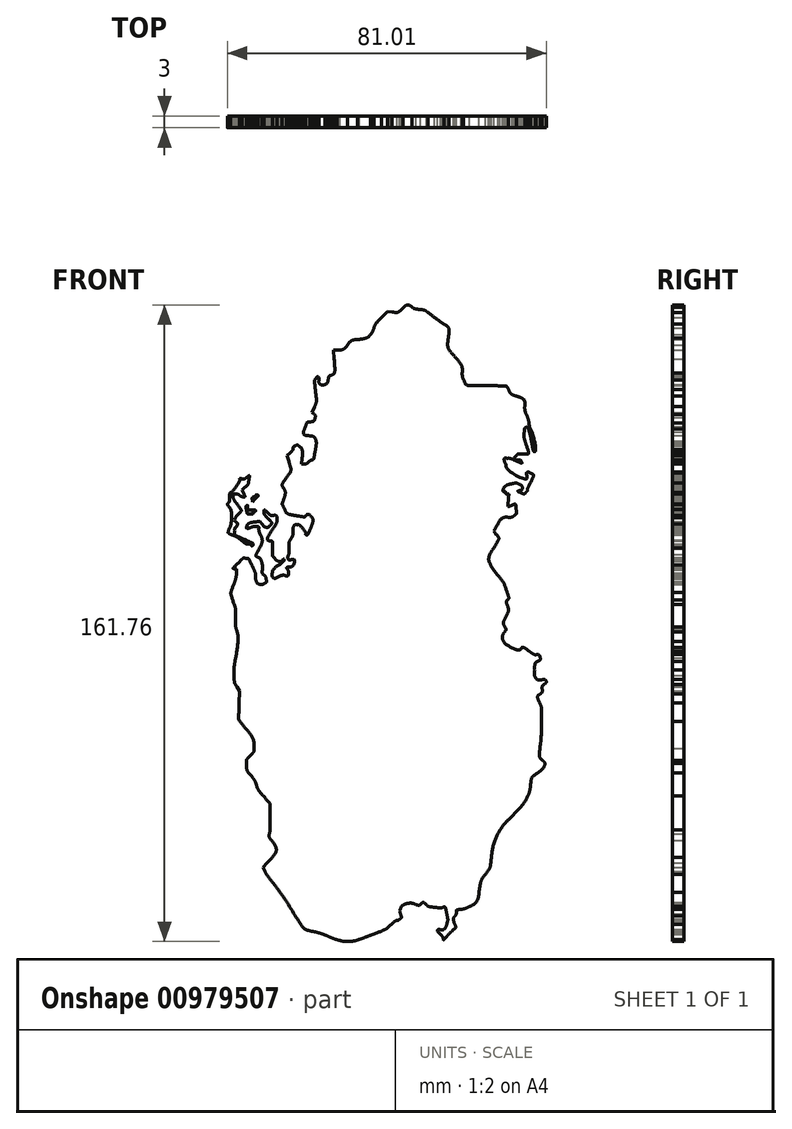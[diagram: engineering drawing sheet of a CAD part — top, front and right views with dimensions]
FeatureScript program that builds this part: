
annotation { "Feature Type Name" : "Feature", "Feature Type Description" : "" }
export const myFeature = defineFeature(function(context is Context, id is Id, definition is map)
    precondition{}
    {
        {
            var Q0;
            Q0=qCreatedBy(makeId("Front.planeOp"),FACE);
            var sketch = newSketch(context, id + "F0", { "sketchPlane" : qUnion([Q0])});
            skLineSegment(sketch, "E0", {"start": v(-32.88, 19.2) * mm, "end": v(-32.1, 20.83) * mm});
            skLineSegment(sketch, "E1", {"start": v(-32.1, 20.83) * mm, "end": v(-32.57, 22.16) * mm});
            skLineSegment(sketch, "E2", {"start": v(-27.5, 16.63) * mm, "end": v(-26.83, 16.28) * mm});
            skLineSegment(sketch, "E3", {"start": v(-26.83, 16.28) * mm, "end": v(-26.97, 16.83) * mm});
            skLineSegment(sketch, "E4", {"start": v(-24.85, 15.67) * mm, "end": v(-25.4, 15.88) * mm});
            skLineSegment(sketch, "E5", {"start": v(-25.4, 15.88) * mm, "end": v(-25.34, 18.4) * mm});
            skLineSegment(sketch, "E6", {"start": v(-1.75, 78.04) * mm, "end": v(-0.2, 79.6) * mm});
            skLineSegment(sketch, "E7", {"start": v(-0.2, 79.6) * mm, "end": v(1.27, 79.6) * mm});
            skLineSegment(sketch, "E8", {"start": v(38.3, 44.26) * mm, "end": v(38.3, 43.17) * mm});
            skLineSegment(sketch, "E9", {"start": v(38.3, 43.17) * mm, "end": v(37.62, 43.24) * mm});
            skLineSegment(sketch, "E10", {"start": v(39.65, -31.25) * mm, "end": v(39.52, -33.83) * mm});
            skLineSegment(sketch, "E11", {"start": v(39.52, -33.83) * mm, "end": v(40.18, -34.42) * mm});
            skLineSegment(sketch, "E12", {"start": v(1.4, 79.08) * mm, "end": v(0.3, 79.22) * mm});
            skLineSegment(sketch, "E13", {"start": v(0.3, 79.22) * mm, "end": v(-1.23, 77.67) * mm});
            skLineSegment(sketch, "E14", {"start": v(-12.51, 69.45) * mm, "end": v(-13.4, 69.45) * mm});
            skLineSegment(sketch, "E15", {"start": v(-13.4, 69.45) * mm, "end": v(-13.27, 67.07) * mm});
            skLineSegment(sketch, "E16", {"start": v(-18.31, 54.9) * mm, "end": v(-18.88, 53.48) * mm});
            skLineSegment(sketch, "E17", {"start": v(-18.88, 53.48) * mm, "end": v(-18.43, 53.1) * mm});
            skLineSegment(sketch, "E18", {"start": v(-20.94, 40.45) * mm, "end": v(-21.55, 40.45) * mm});
            skLineSegment(sketch, "E19", {"start": v(-21.55, 40.45) * mm, "end": v(-21.44, 41.8) * mm});
            skLineSegment(sketch, "E20", {"start": v(-24.47, 43.3) * mm, "end": v(-25.23, 42.61) * mm});
            skLineSegment(sketch, "E21", {"start": v(-25.23, 42.61) * mm, "end": v(-24.8, 41.05) * mm});
            skLineSegment(sketch, "E22", {"start": v(-37.96, -16.18) * mm, "end": v(-37.29, -17.23) * mm});
            skLineSegment(sketch, "E23", {"start": v(-37.29, -17.23) * mm, "end": v(-37.41, -20.41) * mm});
            skLineSegment(sketch, "E24", {"start": v(-30.4, -60.92) * mm, "end": v(-31.42, -62.04) * mm});
            skLineSegment(sketch, "E25", {"start": v(-31.42, -62.04) * mm, "end": v(-30.9, -63.02) * mm});
            skLineSegment(sketch, "E26", {"start": v(-36.35, 33.14) * mm, "end": v(-36.7, 33.88) * mm});
            skLineSegment(sketch, "E27", {"start": v(-36.7, 33.88) * mm, "end": v(-35.92, 34.57) * mm});
            skLineSegment(sketch, "E28", {"start": v(-34.09, 31.43) * mm, "end": v(-34.09, 30.84) * mm});
            skLineSegment(sketch, "E29", {"start": v(-34.09, 30.84) * mm, "end": v(-33.35, 31.56) * mm});
            skFitSpline(sketch, "E30", {"points": [v(-13.45, -80.7) * mm, v(-14.26, -80.4) * mm, v(-15.79, -79.86) * mm, v(-16.84, -79.51) * mm]});
            skFitSpline(sketch, "E31", {"points": [v(-16.84, -79.51) * mm, v(-20.43, -78.33) * mm, v(-20.6, -78.25) * mm, v(-21.55, -77.26) * mm]});
            skFitSpline(sketch, "E32", {"points": [v(-21.55, -77.26) * mm, v(-22.07, -76.72) * mm, v(-23.66, -74.52) * mm, v(-25.09, -72.37) * mm]});
            skFitSpline(sketch, "E33", {"points": [v(-25.09, -72.37) * mm, v(-26.52, -70.21) * mm, v(-28.36, -67.6) * mm, v(-29.19, -66.55) * mm]});
            skFitSpline(sketch, "E34", {"points": [v(-29.19, -66.55) * mm, v(-30.6, -64.76) * mm, v(-31.97, -62.53) * mm, v(-31.97, -62.03) * mm]});
            skFitSpline(sketch, "E35", {"points": [v(-31.97, -62.03) * mm, v(-31.97, -61.91) * mm, v(-31.5, -61.27) * mm, v(-30.92, -60.6) * mm]});
            skFitSpline(sketch, "E36", {"points": [v(-30.92, -60.6) * mm, v(-29.85, -59.39) * mm, v(-29, -57.92) * mm, v(-29, -57.28) * mm]});
            skFitSpline(sketch, "E37", {"points": [v(-29, -57.28) * mm, v(-29, -57.08) * mm, v(-29.34, -56.3) * mm, v(-29.75, -55.53) * mm]});
            skFitSpline(sketch, "E38", {"points": [v(-29.75, -55.53) * mm, v(-30.57, -53.98) * mm, v(-30.63, -53.57) * mm, v(-30.2, -52.72) * mm]});
            skFitSpline(sketch, "E39", {"points": [v(-30.2, -52.72) * mm, v(-29.95, -52.26) * mm, v(-29.92, -51.55) * mm, v(-30.04, -49.29) * mm]});
            skFitSpline(sketch, "E40", {"points": [v(-30.04, -49.29) * mm, v(-30.2, -46.13) * mm, v(-30.12, -46.32) * mm, v(-32.34, -43.6) * mm]});
            skFitSpline(sketch, "E41", {"points": [v(-32.34, -43.6) * mm, v(-32.83, -43) * mm, v(-33.38, -42.01) * mm, v(-33.55, -41.42) * mm]});
            skFitSpline(sketch, "E42", {"points": [v(-33.55, -41.42) * mm, v(-33.73, -40.84) * mm, v(-34.2, -39.94) * mm, v(-34.62, -39.44) * mm]});
            skFitSpline(sketch, "E43", {"points": [v(-34.62, -39.44) * mm, v(-36.03, -37.71) * mm, v(-36.52, -35.97) * mm, v(-35.98, -34.56) * mm]});
            skFitSpline(sketch, "E44", {"points": [v(-35.98, -34.56) * mm, v(-35.86, -34.24) * mm, v(-35.38, -33.57) * mm, v(-34.92, -33.07) * mm]});
            skFitSpline(sketch, "E45", {"points": [v(-34.92, -33.07) * mm, v(-33.97, -32.03) * mm, v(-34, -32.17) * mm, v(-34.37, -30.78) * mm]});
            skFitSpline(sketch, "E46", {"points": [v(-34.37, -30.78) * mm, v(-34.75, -29.38) * mm, v(-35.2, -28.53) * mm, v(-36.46, -26.88) * mm]});
            skFitSpline(sketch, "E47", {"points": [v(-36.46, -26.88) * mm, v(-37.04, -26.13) * mm, v(-37.61, -25.27) * mm, v(-37.73, -24.97) * mm]});
            skFitSpline(sketch, "E48", {"points": [v(-37.73, -24.97) * mm, v(-37.97, -24.39) * mm, v(-38.06, -21.07) * mm, v(-37.9, -18.8) * mm]});
            skFitSpline(sketch, "E49", {"points": [v(-37.9, -18.8) * mm, v(-37.82, -17.55) * mm, v(-37.87, -17.35) * mm, v(-38.39, -16.67) * mm]});
            skFitSpline(sketch, "E50", {"points": [v(-38.39, -16.67) * mm, v(-39.51, -15.19) * mm, v(-39.6, -12.77) * mm, v(-38.72, -7.81) * mm]});
            skFitSpline(sketch, "E51", {"points": [v(-38.72, -7.81) * mm, v(-38.24, -5.14) * mm, v(-38.31, -2.1) * mm, v(-38.87, -1) * mm]});
            skFitSpline(sketch, "E52", {"points": [v(-38.87, -1) * mm, v(-39.1, -0.56) * mm, v(-39.11, -0.29) * mm, v(-38.94, 0.17) * mm]});
            skFitSpline(sketch, "E53", {"points": [v(-38.94, 0.17) * mm, v(-38.62, 1) * mm, v(-38.87, 3.38) * mm, v(-39.5, 5.38) * mm]});
            skFitSpline(sketch, "E54", {"points": [v(-39.5, 5.38) * mm, v(-39.78, 6.29) * mm, v(-40.01, 7.26) * mm, v(-40.01, 7.54) * mm]});
            skFitSpline(sketch, "E55", {"points": [v(-40.01, 7.54) * mm, v(-40.01, 7.83) * mm, v(-39.68, 9.05) * mm, v(-39.27, 10.27) * mm]});
            skFitSpline(sketch, "E56", {"points": [v(-39.27, 10.27) * mm, v(-38.41, 12.85) * mm, v(-38.39, 13.06) * mm, v(-38.96, 13.2) * mm]});
            skFitSpline(sketch, "E57", {"points": [v(-38.96, 13.2) * mm, v(-39.71, 13.4) * mm, v(-39.48, 14.32) * mm, v(-38.38, 15.5) * mm]});
            skFitSpline(sketch, "E58", {"points": [v(-38.38, 15.5) * mm, v(-36.83, 17.16) * mm, v(-35.68, 17.57) * mm, v(-34.74, 16.8) * mm]});
            skFitSpline(sketch, "E59", {"points": [v(-34.74, 16.8) * mm, v(-34.08, 16.26) * mm, v(-32.77, 13.22) * mm, v(-32.66, 11.98) * mm]});
            skFitSpline(sketch, "E60", {"points": [v(-32.66, 11.98) * mm, v(-32.55, 10.86) * mm, v(-32.37, 10.61) * mm, v(-31.6, 10.6) * mm]});
            skFitSpline(sketch, "E61", {"points": [v(-31.6, 10.6) * mm, v(-31, 10.6) * mm, v(-30.96, 11.24) * mm, v(-31.55, 11.77) * mm]});
            skFitSpline(sketch, "E62", {"points": [v(-31.55, 11.77) * mm, v(-31.84, 12.03) * mm, v(-31.97, 12.42) * mm, v(-31.97, 13) * mm]});
            skFitSpline(sketch, "E63", {"points": [v(-31.97, 13) * mm, v(-31.97, 14.32) * mm, v(-32.62, 16.12) * mm, v(-33.18, 16.38) * mm]});
            skFitSpline(sketch, "E64", {"points": [v(-33.18, 16.38) * mm, v(-33.86, 16.69) * mm, v(-33.8, 17.27) * mm, v(-32.88, 19.2) * mm]});
            skFitSpline(sketch, "E65", {"points": [v(-32.57, 22.16) * mm, v(-32.82, 22.9) * mm, v(-33.03, 23.65) * mm, v(-33.03, 23.83) * mm]});
            skFitSpline(sketch, "E66", {"points": [v(-33.03, 23.83) * mm, v(-33.03, 24.1) * mm, v(-33.14, 24.14) * mm, v(-33.5, 24.01) * mm]});
            skFitSpline(sketch, "E67", {"points": [v(-33.5, 24.01) * mm, v(-33.77, 23.92) * mm, v(-34.4, 23.84) * mm, v(-34.93, 23.84) * mm]});
            skFitSpline(sketch, "E68", {"points": [v(-34.93, 23.84) * mm, v(-35.84, 23.83) * mm, v(-35.89, 23.86) * mm, v(-35.95, 24.48) * mm]});
            skFitSpline(sketch, "E69", {"points": [v(-35.95, 24.48) * mm, v(-36.05, 25.55) * mm, v(-34.78, 26.27) * mm, v(-32.78, 26.27) * mm]});
            skFitSpline(sketch, "E70", {"points": [v(-32.78, 26.27) * mm, v(-31.93, 26.27) * mm, v(-31.64, 26.16) * mm, v(-31.1, 25.65) * mm]});
            skFitSpline(sketch, "E71", {"points": [v(-31.1, 25.65) * mm, v(-30.75, 25.3) * mm, v(-30.32, 25.08) * mm, v(-30.15, 25.14) * mm]});
            skFitSpline(sketch, "E72", {"points": [v(-30.15, 25.14) * mm, v(-29.7, 25.31) * mm, v(-29.77, 25.47) * mm, v(-30.7, 26.37) * mm]});
            skFitSpline(sketch, "E73", {"points": [v(-30.7, 26.37) * mm, v(-31.5, 27.15) * mm, v(-31.55, 27.27) * mm, v(-31.55, 28.43) * mm]});
            skFitSpline(sketch, "E74", {"points": [v(-31.55, 28.43) * mm, v(-31.55, 29.6) * mm, v(-31.52, 29.65) * mm, v(-31.02, 29.65) * mm]});
            skFitSpline(sketch, "E75", {"points": [v(-31.02, 29.65) * mm, v(-30.7, 29.65) * mm, v(-30.49, 29.53) * mm, v(-30.49, 29.36) * mm]});
            skFitSpline(sketch, "E76", {"points": [v(-30.49, 29.36) * mm, v(-30.49, 28.94) * mm, v(-28.82, 27.75) * mm, v(-28.24, 27.75) * mm]});
            skFitSpline(sketch, "E77", {"points": [v(-28.24, 27.75) * mm, v(-27.83, 27.75) * mm, v(-27.75, 27.6) * mm, v(-27.62, 26.6) * mm]});
            skFitSpline(sketch, "E78", {"points": [v(-27.62, 26.6) * mm, v(-27.46, 25.26) * mm, v(-27.66, 24.55) * mm, v(-28.57, 23.22) * mm]});
            skFitSpline(sketch, "E79", {"points": [v(-28.57, 23.22) * mm, v(-29.21, 22.29) * mm, v(-29.4, 21.61) * mm, v(-29.02, 21.61) * mm]});
            skFitSpline(sketch, "E80", {"points": [v(-29.02, 21.61) * mm, v(-28.66, 21.61) * mm, v(-28.35, 20.18) * mm, v(-28.49, 19.14) * mm]});
            skFitSpline(sketch, "E81", {"points": [v(-28.49, 19.14) * mm, v(-28.66, 17.84) * mm, v(-28.36, 17.07) * mm, v(-27.5, 16.63) * mm]});
            skFitSpline(sketch, "E82", {"points": [v(-26.97, 16.83) * mm, v(-27.1, 17.33) * mm, v(-27.05, 17.38) * mm, v(-26.5, 17.38) * mm]});
            skFitSpline(sketch, "E83", {"points": [v(-26.5, 17.38) * mm, v(-25.81, 17.38) * mm, v(-25.62, 17.08) * mm, v(-25.62, 16.04) * mm]});
            skFitSpline(sketch, "E84", {"points": [v(-25.62, 16.04) * mm, v(-25.62, 15.5) * mm, v(-25.82, 15.19) * mm, v(-26.56, 14.52) * mm]});
            skFitSpline(sketch, "E85", {"points": [v(-26.56, 14.52) * mm, v(-27.09, 14.05) * mm, v(-27.58, 13.4) * mm, v(-27.66, 13.06) * mm]});
            skFitSpline(sketch, "E86", {"points": [v(-27.66, 13.06) * mm, v(-27.79, 12.49) * mm, v(-27.76, 12.45) * mm, v(-27.3, 12.58) * mm]});
            skFitSpline(sketch, "E87", {"points": [v(-27.3, 12.58) * mm, v(-27.01, 12.65) * mm, v(-26.47, 12.72) * mm, v(-26.09, 12.72) * mm]});
            skFitSpline(sketch, "E88", {"points": [v(-26.09, 12.72) * mm, v(-25.47, 12.72) * mm, v(-25.42, 12.76) * mm, v(-25.61, 13.13) * mm]});
            skFitSpline(sketch, "E89", {"points": [v(-25.61, 13.13) * mm, v(-26.02, 13.88) * mm, v(-25.88, 14.6) * mm, v(-25.31, 14.75) * mm]});
            skFitSpline(sketch, "E90", {"points": [v(-25.31, 14.75) * mm, v(-25.03, 14.82) * mm, v(-24.68, 15.01) * mm, v(-24.55, 15.17) * mm]});
            skFitSpline(sketch, "E91", {"points": [v(-24.55, 15.17) * mm, v(-24.35, 15.4) * mm, v(-24.42, 15.5) * mm, v(-24.85, 15.67) * mm]});
            skFitSpline(sketch, "E92", {"points": [v(-25.34, 18.4) * mm, v(-25.28, 20.49) * mm, v(-25.2, 21.05) * mm, v(-24.84, 21.66) * mm]});
            skFitSpline(sketch, "E93", {"points": [v(-24.84, 21.66) * mm, v(-24.6, 22.07) * mm, v(-24.33, 22.91) * mm, v(-24.25, 23.54) * mm]});
            skFitSpline(sketch, "E94", {"points": [v(-24.25, 23.54) * mm, v(-24.05, 24.98) * mm, v(-23.67, 25.42) * mm, v(-22.64, 25.42) * mm]});
            skFitSpline(sketch, "E95", {"points": [v(-22.64, 25.42) * mm, v(-21.97, 25.42) * mm, v(-21.73, 25.28) * mm, v(-21.09, 24.54) * mm]});
            skFitSpline(sketch, "E96", {"points": [v(-21.09, 24.54) * mm, v(-20.67, 24.05) * mm, v(-20.32, 23.55) * mm, v(-20.32, 23.43) * mm]});
            skFitSpline(sketch, "E97", {"points": [v(-20.32, 23.43) * mm, v(-20.3, 22.93) * mm, v(-19.5, 25.15) * mm, v(-19.5, 25.74) * mm]});
            skFitSpline(sketch, "E98", {"points": [v(-19.5, 25.74) * mm, v(-19.48, 26.68) * mm, v(-19.75, 27) * mm, v(-20.27, 26.68) * mm]});
            skFitSpline(sketch, "E99", {"points": [v(-20.27, 26.68) * mm, v(-20.84, 26.32) * mm, v(-23.7, 26.75) * mm, v(-24.99, 27.38) * mm]});
            skFitSpline(sketch, "E100", {"points": [v(-24.99, 27.38) * mm, v(-26.7, 28.23) * mm, v(-27.27, 29.95) * mm, v(-26.55, 32.07) * mm]});
            skFitSpline(sketch, "E101", {"points": [v(-26.55, 32.07) * mm, v(-26.23, 33) * mm, v(-26.23, 33.13) * mm, v(-26.58, 33.9) * mm]});
            skFitSpline(sketch, "E102", {"points": [v(-26.58, 33.9) * mm, v(-27.04, 34.91) * mm, v(-26.9, 36) * mm, v(-26.2, 36.92) * mm]});
            skFitSpline(sketch, "E103", {"points": [v(-26.2, 36.92) * mm, v(-24.96, 38.54) * mm, v(-24.76, 39.42) * mm, v(-25.3, 40.73) * mm]});
            skFitSpline(sketch, "E104", {"points": [v(-25.3, 40.73) * mm, v(-25.48, 41.15) * mm, v(-25.62, 41.87) * mm, v(-25.62, 42.33) * mm]});
            skFitSpline(sketch, "E105", {"points": [v(-25.62, 42.33) * mm, v(-25.62, 43.02) * mm, v(-25.5, 43.25) * mm, v(-24.99, 43.62) * mm]});
            skFitSpline(sketch, "E106", {"points": [v(-24.99, 43.62) * mm, v(-24.64, 43.87) * mm, v(-24.35, 44.26) * mm, v(-24.35, 44.48) * mm]});
            skFitSpline(sketch, "E107", {"points": [v(-24.35, 44.48) * mm, v(-24.35, 45.6) * mm, v(-22.43, 46.16) * mm, v(-21.62, 45.29) * mm]});
            skFitSpline(sketch, "E108", {"points": [v(-21.62, 45.29) * mm, v(-21.1, 44.74) * mm, v(-20.66, 42.78) * mm, v(-20.82, 41.8) * mm]});
            skFitSpline(sketch, "E109", {"points": [v(-20.82, 41.8) * mm, v(-20.95, 40.98) * mm, v(-20.5, 40.8) * mm, v(-20.12, 41.5) * mm]});
            skFitSpline(sketch, "E110", {"points": [v(-20.12, 41.5) * mm, v(-20, 41.74) * mm, v(-19.7, 41.93) * mm, v(-19.48, 41.93) * mm]});
            skFitSpline(sketch, "E111", {"points": [v(-19.48, 41.93) * mm, v(-19.2, 41.93) * mm, v(-19.03, 42.12) * mm, v(-18.95, 42.51) * mm]});
            skFitSpline(sketch, "E112", {"points": [v(-18.95, 42.51) * mm, v(-18.9, 42.83) * mm, v(-18.75, 43.5) * mm, v(-18.63, 44) * mm]});
            skFitSpline(sketch, "E113", {"points": [v(-18.63, 44) * mm, v(-18.15, 46.1) * mm, v(-18.46, 46.83) * mm, v(-19.95, 47.1) * mm]});
            skFitSpline(sketch, "E114", {"points": [v(-19.95, 47.1) * mm, v(-21.37, 47.35) * mm, v(-21.68, 48.31) * mm, v(-21.02, 50.45) * mm]});
            skFitSpline(sketch, "E115", {"points": [v(-21.02, 50.45) * mm, v(-20.67, 51.58) * mm, v(-20.6, 51.66) * mm, v(-20, 51.67) * mm]});
            skFitSpline(sketch, "E116", {"points": [v(-20, 51.67) * mm, v(-19.64, 51.67) * mm, v(-19.17, 51.8) * mm, v(-18.94, 51.97) * mm]});
            skFitSpline(sketch, "E117", {"points": [v(-18.94, 51.97) * mm, v(-18.56, 52.25) * mm, v(-18.55, 52.28) * mm, v(-18.9, 52.67) * mm]});
            skFitSpline(sketch, "E118", {"points": [v(-18.9, 52.67) * mm, v(-19.36, 53.18) * mm, v(-19.37, 53.99) * mm, v(-18.93, 55) * mm]});
            skFitSpline(sketch, "E119", {"points": [v(-18.93, 55) * mm, v(-18.26, 56.57) * mm, v(-18.22, 56.96) * mm, v(-18.55, 58.71) * mm]});
            skFitSpline(sketch, "E120", {"points": [v(-18.55, 58.71) * mm, v(-19.05, 61.35) * mm, v(-18.66, 63.1) * mm, v(-17.57, 63.1) * mm]});
            skFitSpline(sketch, "E121", {"points": [v(-17.57, 63.1) * mm, v(-17.13, 63.1) * mm, v(-16.93, 62.86) * mm, v(-16.62, 61.94) * mm]});
            skFitSpline(sketch, "E122", {"points": [v(-16.62, 61.94) * mm, v(-16.19, 60.62) * mm, v(-15.25, 61.36) * mm, v(-15.25, 63.03) * mm]});
            skFitSpline(sketch, "E123", {"points": [v(-15.25, 63.03) * mm, v(-15.25, 63.72) * mm, v(-15.21, 63.77) * mm, v(-14.72, 63.65) * mm]});
            skFitSpline(sketch, "E124", {"points": [v(-14.72, 63.65) * mm, v(-13.88, 63.44) * mm, v(-13.7, 64.21) * mm, v(-13.86, 67.25) * mm]});
            skFitSpline(sketch, "E125", {"points": [v(-13.86, 67.25) * mm, v(-14.01, 70.15) * mm, v(-14.06, 70.07) * mm, v(-12.21, 70.08) * mm]});
            skFitSpline(sketch, "E126", {"points": [v(-12.21, 70.08) * mm, v(-11.52, 70.08) * mm, v(-11.25, 70.23) * mm, v(-10.4, 71.12) * mm]});
            skFitSpline(sketch, "E127", {"points": [v(-10.4, 71.12) * mm, v(-9.38, 72.18) * mm, v(-9.03, 72.34) * mm, v(-6.52, 72.84) * mm]});
            skFitSpline(sketch, "E128", {"points": [v(-6.52, 72.84) * mm, v(-4.93, 73.15) * mm, v(-4.21, 73.78) * mm, v(-3.7, 75.27) * mm]});
            skFitSpline(sketch, "E129", {"points": [v(-3.7, 75.27) * mm, v(-3.38, 76.2) * mm, v(-2.96, 76.8) * mm, v(-1.75, 78.04) * mm]});
            skFitSpline(sketch, "E130", {"points": [v(1.27, 79.6) * mm, v(2.66, 79.6) * mm, v(2.79, 79.65) * mm, v(3.57, 80.36) * mm]});
            skFitSpline(sketch, "E131", {"points": [v(3.57, 80.36) * mm, v(4.72, 81.4) * mm, v(5.62, 81.51) * mm, v(6.84, 80.8) * mm]});
            skFitSpline(sketch, "E132", {"points": [v(6.84, 80.8) * mm, v(7.4, 80.48) * mm, v(8.11, 80.24) * mm, v(8.56, 80.24) * mm]});
            skFitSpline(sketch, "E133", {"points": [v(8.56, 80.24) * mm, v(9.65, 80.24) * mm, v(10.66, 79.76) * mm, v(12.03, 78.58) * mm]});
            skFitSpline(sketch, "E134", {"points": [v(12.03, 78.58) * mm, v(12.68, 78.02) * mm, v(13.76, 77.21) * mm, v(14.43, 76.8) * mm]});
            skFitSpline(sketch, "E135", {"points": [v(14.43, 76.8) * mm, v(16.07, 75.75) * mm, v(16.3, 75.23) * mm, v(16.26, 72.68) * mm]});
            skFitSpline(sketch, "E136", {"points": [v(16.26, 72.68) * mm, v(16.21, 70.3) * mm, v(16.3, 70.06) * mm, v(17.99, 67.97) * mm]});
            skFitSpline(sketch, "E137", {"points": [v(17.99, 67.97) * mm, v(19.34, 66.28) * mm, v(19.58, 65.73) * mm, v(19.78, 63.84) * mm]});
            skFitSpline(sketch, "E138", {"points": [v(19.78, 63.84) * mm, v(19.97, 61.97) * mm, v(20.1, 61.75) * mm, v(21.2, 61.28) * mm]});
            skFitSpline(sketch, "E139", {"points": [v(21.2, 61.28) * mm, v(21.95, 60.97) * mm, v(22.77, 60.9) * mm, v(25.95, 60.87) * mm]});
            skFitSpline(sketch, "E140", {"points": [v(25.95, 60.87) * mm, v(29.47, 60.83) * mm, v(29.87, 60.8) * mm, v(30.78, 60.35) * mm]});
            skFitSpline(sketch, "E141", {"points": [v(30.78, 60.35) * mm, v(31.33, 60.09) * mm, v(31.82, 59.71) * mm, v(31.88, 59.53) * mm]});
            skFitSpline(sketch, "E142", {"points": [v(31.88, 59.53) * mm, v(32.1, 58.78) * mm, v(32.32, 58.58) * mm, v(33.34, 58.19) * mm]});
            skFitSpline(sketch, "E143", {"points": [v(33.34, 58.19) * mm, v(35, 57.54) * mm, v(35.47, 56.96) * mm, v(35.61, 55.41) * mm]});
            skFitSpline(sketch, "E144", {"points": [v(35.61, 55.41) * mm, v(35.68, 54.7) * mm, v(35.93, 53.67) * mm, v(36.17, 53.15) * mm]});
            skFitSpline(sketch, "E145", {"points": [v(36.17, 53.15) * mm, v(36.4, 52.63) * mm, v(36.6, 51.94) * mm, v(36.6, 51.62) * mm]});
            skFitSpline(sketch, "E146", {"points": [v(36.6, 51.62) * mm, v(36.6, 51.3) * mm, v(36.8, 50.55) * mm, v(37.02, 49.93) * mm]});
            skFitSpline(sketch, "E147", {"points": [v(37.02, 49.93) * mm, v(37.7, 48.08) * mm, v(38.3, 45.42) * mm, v(38.3, 44.26) * mm]});
            skFitSpline(sketch, "E148", {"points": [v(37.62, 43.24) * mm, v(36.87, 43.31) * mm, v(36.86, 43.33) * mm, v(36.05, 46.9) * mm]});
            skFitSpline(sketch, "E149", {"points": [v(36.05, 46.9) * mm, v(35.75, 48.23) * mm, v(35.65, 48.45) * mm, v(35.6, 47.92) * mm]});
            skFitSpline(sketch, "E150", {"points": [v(35.6, 47.92) * mm, v(35.56, 47.55) * mm, v(35.72, 46.61) * mm, v(35.96, 45.84) * mm]});
            skFitSpline(sketch, "E151", {"points": [v(35.96, 45.84) * mm, v(36.2, 45.06) * mm, v(36.4, 44.16) * mm, v(36.4, 43.83) * mm]});
            skFitSpline(sketch, "E152", {"points": [v(36.4, 43.83) * mm, v(36.4, 42.72) * mm, v(36.23, 42.57) * mm, v(35.04, 42.57) * mm]});
            skFitSpline(sketch, "E153", {"points": [v(35.04, 42.57) * mm, v(34.35, 42.57) * mm, v(33.78, 42.44) * mm, v(33.53, 42.23) * mm]});
            skFitSpline(sketch, "E154", {"points": [v(33.53, 42.23) * mm, v(33.14, 41.92) * mm, v(33.15, 41.9) * mm, v(33.78, 42.01) * mm]});
            skFitSpline(sketch, "E155", {"points": [v(33.78, 42.01) * mm, v(34.37, 42.1) * mm, v(34.48, 42.05) * mm, v(34.7, 41.5) * mm]});
            skFitSpline(sketch, "E156", {"points": [v(34.7, 41.5) * mm, v(35.23, 40.23) * mm, v(34.46, 39.89) * mm, v(32.77, 40.66) * mm]});
            skFitSpline(sketch, "E157", {"points": [v(32.77, 40.66) * mm, v(30, 41.91) * mm, v(30.46, 40.26) * mm, v(33.3, 38.77) * mm]});
            skFitSpline(sketch, "E158", {"points": [v(33.3, 38.77) * mm, v(34.7, 38.04) * mm, v(35.03, 37.98) * mm, v(35.2, 38.44) * mm]});
            skFitSpline(sketch, "E159", {"points": [v(35.2, 38.44) * mm, v(35.4, 38.97) * mm, v(36.94, 38.86) * mm, v(37.34, 38.29) * mm]});
            skFitSpline(sketch, "E160", {"points": [v(37.34, 38.29) * mm, v(37.8, 37.64) * mm, v(37.75, 36.5) * mm, v(37.25, 35.69) * mm]});
            skFitSpline(sketch, "E161", {"points": [v(37.25, 35.69) * mm, v(37.01, 35.31) * mm, v(36.68, 34.6) * mm, v(36.5, 34.09) * mm]});
            skFitSpline(sketch, "E162", {"points": [v(36.5, 34.09) * mm, v(36.07, 32.87) * mm, v(35.62, 32.4) * mm, v(34.86, 32.4) * mm]});
            skFitSpline(sketch, "E163", {"points": [v(34.86, 32.4) * mm, v(34.06, 32.4) * mm, v(32.85, 32.98) * mm, v(32.57, 33.5) * mm]});
            skFitSpline(sketch, "E164", {"points": [v(32.57, 33.5) * mm, v(32.35, 33.9) * mm, v(32.37, 33.91) * mm, v(33.4, 34.23) * mm]});
            skFitSpline(sketch, "E165", {"points": [v(33.4, 34.23) * mm, v(33.55, 34.27) * mm, v(33.64, 34.43) * mm, v(33.6, 34.58) * mm]});
            skFitSpline(sketch, "E166", {"points": [v(33.6, 34.58) * mm, v(33.47, 34.97) * mm, v(32.1, 35.02) * mm, v(31.26, 34.66) * mm]});
            skFitSpline(sketch, "E167", {"points": [v(31.26, 34.66) * mm, v(30.63, 34.4) * mm, v(30.54, 34.27) * mm, v(30.63, 33.8) * mm]});
            skFitSpline(sketch, "E168", {"points": [v(30.63, 33.8) * mm, v(30.71, 33.37) * mm, v(30.83, 33.27) * mm, v(31.13, 33.37) * mm]});
            skFitSpline(sketch, "E169", {"points": [v(31.13, 33.37) * mm, v(31.68, 33.54) * mm, v(31.8, 33.13) * mm, v(31.57, 31.7) * mm]});
            skFitSpline(sketch, "E170", {"points": [v(31.57, 31.7) * mm, v(31.47, 31.04) * mm, v(31.4, 30.5) * mm, v(31.43, 30.5) * mm]});
            skFitSpline(sketch, "E171", {"points": [v(31.43, 30.5) * mm, v(31.46, 30.5) * mm, v(31.82, 30.65) * mm, v(32.25, 30.82) * mm]});
            skFitSpline(sketch, "E172", {"points": [v(32.25, 30.82) * mm, v(33.01, 31.14) * mm, v(33.02, 31.14) * mm, v(33.26, 30.56) * mm]});
            skFitSpline(sketch, "E173", {"points": [v(33.26, 30.56) * mm, v(33.39, 30.24) * mm, v(33.5, 29.43) * mm, v(33.52, 28.77) * mm]});
            skFitSpline(sketch, "E174", {"points": [v(33.52, 28.77) * mm, v(33.55, 27.14) * mm, v(33.03, 26.57) * mm, v(31.4, 26.43) * mm]});
            skFitSpline(sketch, "E175", {"points": [v(31.4, 26.43) * mm, v(29.99, 26.32) * mm, v(29.27, 25.83) * mm, v(28.59, 24.5) * mm]});
            skFitSpline(sketch, "E176", {"points": [v(28.59, 24.5) * mm, v(28.09, 23.52) * mm, v(28.09, 23.5) * mm, v(28.46, 22.8) * mm]});
            skFitSpline(sketch, "E177", {"points": [v(28.46, 22.8) * mm, v(29.02, 21.76) * mm, v(28.8, 20.5) * mm, v(27.76, 18.77) * mm]});
            skFitSpline(sketch, "E178", {"points": [v(27.76, 18.77) * mm, v(26.26, 16.28) * mm, v(26.34, 15.6) * mm, v(28.5, 12.89) * mm]});
            skFitSpline(sketch, "E179", {"points": [v(28.5, 12.89) * mm, v(30.07, 10.9) * mm, v(30.64, 9.85) * mm, v(31.32, 7.7) * mm]});
            skFitSpline(sketch, "E180", {"points": [v(31.32, 7.7) * mm, v(31.79, 6.2) * mm, v(31.8, 6.14) * mm, v(31.41, 5.73) * mm]});
            skFitSpline(sketch, "E181", {"points": [v(31.41, 5.73) * mm, v(31.08, 5.36) * mm, v(31.06, 5.2) * mm, v(31.28, 4.6) * mm]});
            skFitSpline(sketch, "E182", {"points": [v(31.28, 4.6) * mm, v(31.65, 3.58) * mm, v(31.59, 2.92) * mm, v(31, 1.59) * mm]});
            skFitSpline(sketch, "E183", {"points": [v(31, 1.59) * mm, v(30.4, 0.22) * mm, v(30.37, 0) * mm, v(30.73, -0.98) * mm]});
            skFitSpline(sketch, "E184", {"points": [v(30.73, -0.98) * mm, v(30.96, -1.6) * mm, v(30.93, -1.79) * mm, v(30.48, -2.62) * mm]});
            skFitSpline(sketch, "E185", {"points": [v(30.48, -2.62) * mm, v(29.76, -3.92) * mm, v(30.03, -4.4) * mm, v(31.97, -5.39) * mm]});
            skFitSpline(sketch, "E186", {"points": [v(31.97, -5.39) * mm, v(33.32, -6.07) * mm, v(33.55, -6.12) * mm, v(34.1, -5.9) * mm]});
            skFitSpline(sketch, "E187", {"points": [v(34.1, -5.9) * mm, v(34.89, -5.57) * mm, v(35.48, -5.74) * mm, v(36.67, -6.64) * mm]});
            skFitSpline(sketch, "E188", {"points": [v(36.67, -6.64) * mm, v(37.21, -7.06) * mm, v(37.94, -7.45) * mm, v(38.28, -7.52) * mm]});
            skFitSpline(sketch, "E189", {"points": [v(38.28, -7.52) * mm, v(38.74, -7.61) * mm, v(38.97, -7.82) * mm, v(39.14, -8.29) * mm]});
            skFitSpline(sketch, "E190", {"points": [v(39.14, -8.29) * mm, v(39.46, -9.22) * mm, v(39.43, -9.36) * mm, v(38.73, -10.24) * mm]});
            skFitSpline(sketch, "E191", {"points": [v(38.73, -10.24) * mm, v(37.95, -11.22) * mm, v(37.9, -12.13) * mm, v(38.57, -13.12) * mm]});
            skFitSpline(sketch, "E192", {"points": [v(38.57, -13.12) * mm, v(38.94, -13.67) * mm, v(39.23, -13.86) * mm, v(39.79, -13.91) * mm]});
            skFitSpline(sketch, "E193", {"points": [v(39.79, -13.91) * mm, v(40.2, -13.95) * mm, v(40.6, -14.1) * mm, v(40.68, -14.23) * mm]});
            skFitSpline(sketch, "E194", {"points": [v(40.68, -14.23) * mm, v(40.98, -14.7) * mm, v(40.84, -15.58) * mm, v(40.4, -15.98) * mm]});
            skFitSpline(sketch, "E195", {"points": [v(40.4, -15.98) * mm, v(40.04, -16.3) * mm, v(39.97, -16.56) * mm, v(40.05, -17.26) * mm]});
            skFitSpline(sketch, "E196", {"points": [v(40.05, -17.26) * mm, v(40.14, -18.03) * mm, v(40.09, -18.17) * mm, v(39.65, -18.37) * mm]});
            skFitSpline(sketch, "E197", {"points": [v(39.65, -18.37) * mm, v(39.06, -18.64) * mm, v(39.03, -18.9) * mm, v(39.5, -20) * mm]});
            skFitSpline(sketch, "E198", {"points": [v(39.5, -20) * mm, v(39.77, -20.67) * mm, v(39.83, -21.57) * mm, v(39.81, -24.74) * mm]});
            skFitSpline(sketch, "E199", {"points": [v(39.81, -24.74) * mm, v(39.8, -26.9) * mm, v(39.73, -29.82) * mm, v(39.65, -31.25) * mm]});
            skFitSpline(sketch, "E200", {"points": [v(40.18, -34.42) * mm, v(40.54, -34.74) * mm, v(40.84, -35.18) * mm, v(40.84, -35.41) * mm]});
            skFitSpline(sketch, "E201", {"points": [v(40.84, -35.41) * mm, v(40.84, -36.27) * mm, v(39.96, -37.65) * mm, v(38.92, -38.41) * mm]});
            skFitSpline(sketch, "E202", {"points": [v(38.92, -38.41) * mm, v(37.63, -39.36) * mm, v(37.28, -40) * mm, v(37.05, -41.89) * mm]});
            skFitSpline(sketch, "E203", {"points": [v(37.05, -41.89) * mm, v(36.94, -42.7) * mm, v(36.66, -43.77) * mm, v(36.42, -44.27) * mm]});
            skFitSpline(sketch, "E204", {"points": [v(36.42, -44.27) * mm, v(35.96, -45.22) * mm, v(33.78, -47.87) * mm, v(31.3, -50.5) * mm]});
            skFitSpline(sketch, "E205", {"points": [v(31.3, -50.5) * mm, v(29.02, -52.92) * mm, v(27.8, -55.66) * mm, v(27.2, -59.77) * mm]});
            skFitSpline(sketch, "E206", {"points": [v(27.2, -59.77) * mm, v(26.85, -62.13) * mm, v(26.75, -62.37) * mm, v(25.14, -65) * mm]});
            skFitSpline(sketch, "E207", {"points": [v(25.14, -65) * mm, v(24.58, -65.91) * mm, v(24.35, -66.6) * mm, v(24.16, -67.9) * mm]});
            skFitSpline(sketch, "E208", {"points": [v(24.16, -67.9) * mm, v(23.88, -69.93) * mm, v(23.36, -71.03) * mm, v(22.29, -71.92) * mm]});
            skFitSpline(sketch, "E209", {"points": [v(22.29, -71.92) * mm, v(21.43, -72.63) * mm, v(19.94, -73.22) * mm, v(19, -73.22) * mm]});
            skFitSpline(sketch, "E210", {"points": [v(19, -73.22) * mm, v(18.6, -73.22) * mm, v(18.4, -73.32) * mm, v(18.4, -73.56) * mm]});
            skFitSpline(sketch, "E211", {"points": [v(18.4, -73.56) * mm, v(18.4, -73.75) * mm, v(18.21, -74.22) * mm, v(17.97, -74.6) * mm]});
            skFitSpline(sketch, "E212", {"points": [v(17.97, -74.6) * mm, v(17.57, -75.26) * mm, v(17.56, -75.35) * mm, v(17.87, -76.08) * mm]});
            skFitSpline(sketch, "E213", {"points": [v(17.87, -76.08) * mm, v(18.34, -77.22) * mm, v(18.3, -77.38) * mm, v(17.14, -78.58) * mm]});
            skFitSpline(sketch, "E214", {"points": [v(17.14, -78.58) * mm, v(16.56, -79.18) * mm, v(15.87, -79.93) * mm, v(15.6, -80.25) * mm]});
            skFitSpline(sketch, "E215", {"points": [v(15.6, -80.25) * mm, v(15.34, -80.56) * mm, v(14.86, -80.88) * mm, v(14.54, -80.96) * mm]});
            skFitSpline(sketch, "E216", {"points": [v(14.54, -80.96) * mm, v(14.03, -81.08) * mm, v(13.96, -81.03) * mm, v(13.96, -80.56) * mm]});
            skFitSpline(sketch, "E217", {"points": [v(13.96, -80.56) * mm, v(13.96, -80.25) * mm, v(13.75, -79.86) * mm, v(13.47, -79.63) * mm]});
            skFitSpline(sketch, "E218", {"points": [v(13.47, -79.63) * mm, v(12.33, -78.73) * mm, v(12.3, -77.45) * mm, v(13.44, -77.45) * mm]});
            skFitSpline(sketch, "E219", {"points": [v(13.44, -77.45) * mm, v(14.2, -77.45) * mm, v(15.11, -76) * mm, v(14.94, -75.07) * mm]});
            skFitSpline(sketch, "E220", {"points": [v(14.94, -75.07) * mm, v(14.87, -74.7) * mm, v(14.75, -74.02) * mm, v(14.67, -73.57) * mm]});
            skFitSpline(sketch, "E221", {"points": [v(14.67, -73.57) * mm, v(14.58, -73.02) * mm, v(14.45, -72.8) * mm, v(14.25, -72.88) * mm]});
            skFitSpline(sketch, "E222", {"points": [v(14.25, -72.88) * mm, v(14.1, -72.94) * mm, v(13.13, -72.88) * mm, v(12.11, -72.76) * mm]});
            skFitSpline(sketch, "E223", {"points": [v(12.11, -72.76) * mm, v(10.8, -72.6) * mm, v(10.12, -72.4) * mm, v(9.8, -72.1) * mm]});
            skFitSpline(sketch, "E224", {"points": [v(9.8, -72.1) * mm, v(9.32, -71.67) * mm, v(8.88, -71.75) * mm, v(8.88, -72.28) * mm]});
            skFitSpline(sketch, "E225", {"points": [v(8.88, -72.28) * mm, v(8.88, -72.66) * mm, v(8.5, -72.65) * mm, v(7.82, -72.26) * mm]});
            skFitSpline(sketch, "E226", {"points": [v(7.82, -72.26) * mm, v(7.11, -71.86) * mm, v(5.83, -71.87) * mm, v(4.94, -72.29) * mm]});
            skFitSpline(sketch, "E227", {"points": [v(4.94, -72.29) * mm, v(4.16, -72.66) * mm, v(4.18, -72.61) * mm, v(4.14, -74.27) * mm]});
            skFitSpline(sketch, "E228", {"points": [v(4.14, -74.27) * mm, v(4.12, -75.43) * mm, v(4.11, -75.44) * mm, v(3.17, -75.91) * mm]});
            skFitSpline(sketch, "E229", {"points": [v(3.17, -75.91) * mm, v(2.65, -76.18) * mm, v(1.84, -76.77) * mm, v(1.36, -77.24) * mm]});
            skFitSpline(sketch, "E230", {"points": [v(1.36, -77.24) * mm, v(0.68, -77.91) * mm, v(-0.19, -78.37) * mm, v(-2.67, -79.37) * mm]});
            skFitSpline(sketch, "E231", {"points": [v(-2.67, -79.37) * mm, v(-6.5, -80.92) * mm, v(-7.82, -81.25) * mm, v(-10.17, -81.25) * mm]});
            skFitSpline(sketch, "E232", {"points": [v(-10.17, -81.25) * mm, v(-11.59, -81.25) * mm, v(-12.28, -81.13) * mm, v(-13.45, -80.7) * mm]});
            skFitSpline(sketch, "E233", {"points": [v(-6.84, -80.3) * mm, v(-6.29, -80.14) * mm, v(-4.56, -79.5) * mm, v(-3, -78.88) * mm]});
            skFitSpline(sketch, "E234", {"points": [v(-3, -78.88) * mm, v(-0.66, -77.96) * mm, v(0.05, -77.57) * mm, v(1.08, -76.65) * mm]});
            skFitSpline(sketch, "E235", {"points": [v(1.08, -76.65) * mm, v(1.77, -76.04) * mm, v(2.46, -75.54) * mm, v(2.62, -75.54) * mm]});
            skFitSpline(sketch, "E236", {"points": [v(2.62, -75.54) * mm, v(2.78, -75.54) * mm, v(3.12, -75.37) * mm, v(3.38, -75.16) * mm]});
            skFitSpline(sketch, "E237", {"points": [v(3.38, -75.16) * mm, v(3.8, -74.81) * mm, v(3.83, -74.72) * mm, v(3.59, -73.93) * mm]});
            skFitSpline(sketch, "E238", {"points": [v(3.59, -73.93) * mm, v(3.4, -73.28) * mm, v(3.39, -72.96) * mm, v(3.57, -72.61) * mm]});
            skFitSpline(sketch, "E239", {"points": [v(3.57, -72.61) * mm, v(4.07, -71.69) * mm, v(6.12, -71.11) * mm, v(7.53, -71.5) * mm]});
            skFitSpline(sketch, "E240", {"points": [v(7.53, -71.5) * mm, v(8.17, -71.68) * mm, v(8.4, -71.66) * mm, v(8.68, -71.41) * mm]});
            skFitSpline(sketch, "E241", {"points": [v(8.68, -71.41) * mm, v(9.15, -70.98) * mm, v(9.64, -71.02) * mm, v(10.13, -71.54) * mm]});
            skFitSpline(sketch, "E242", {"points": [v(10.13, -71.54) * mm, v(10.44, -71.88) * mm, v(10.95, -72.03) * mm, v(12.2, -72.17) * mm]});
            skFitSpline(sketch, "E243", {"points": [v(12.2, -72.17) * mm, v(13.1, -72.28) * mm, v(14, -72.32) * mm, v(14.17, -72.26) * mm]});
            skFitSpline(sketch, "E244", {"points": [v(14.17, -72.26) * mm, v(14.75, -72.09) * mm, v(15.04, -72.5) * mm, v(15.33, -73.91) * mm]});
            skFitSpline(sketch, "E245", {"points": [v(15.33, -73.91) * mm, v(15.54, -74.89) * mm, v(15.57, -75.53) * mm, v(15.43, -76.04) * mm]});
            skFitSpline(sketch, "E246", {"points": [v(15.43, -76.04) * mm, v(15.14, -77.06) * mm, v(14.45, -77.87) * mm, v(13.85, -77.87) * mm]});
            skFitSpline(sketch, "E247", {"points": [v(13.85, -77.87) * mm, v(13.06, -77.87) * mm, v(13.01, -78.27) * mm, v(13.7, -79) * mm]});
            skFitSpline(sketch, "E248", {"points": [v(13.7, -79) * mm, v(14.06, -79.37) * mm, v(14.38, -79.86) * mm, v(14.43, -80.1) * mm]});
            skFitSpline(sketch, "E249", {"points": [v(14.43, -80.1) * mm, v(14.5, -80.48) * mm, v(14.55, -80.47) * mm, v(15.03, -79.9) * mm]});
            skFitSpline(sketch, "E250", {"points": [v(15.03, -79.9) * mm, v(15.31, -79.57) * mm, v(16.02, -78.83) * mm, v(16.6, -78.28) * mm]});
            skFitSpline(sketch, "E251", {"points": [v(16.6, -78.28) * mm, v(17.64, -77.28) * mm, v(17.65, -77.26) * mm, v(17.4, -76.55) * mm]});
            skFitSpline(sketch, "E252", {"points": [v(17.4, -76.55) * mm, v(17.05, -75.6) * mm, v(17.07, -74.87) * mm, v(17.45, -74.37) * mm]});
            skFitSpline(sketch, "E253", {"points": [v(17.45, -74.37) * mm, v(17.62, -74.14) * mm, v(17.76, -73.7) * mm, v(17.76, -73.4) * mm]});
            skFitSpline(sketch, "E254", {"points": [v(17.76, -73.4) * mm, v(17.77, -72.89) * mm, v(17.86, -72.83) * mm, v(18.88, -72.7) * mm]});
            skFitSpline(sketch, "E255", {"points": [v(18.88, -72.7) * mm, v(19.5, -72.62) * mm, v(20.47, -72.3) * mm, v(21.04, -71.99) * mm]});
            skFitSpline(sketch, "E256", {"points": [v(21.04, -71.99) * mm, v(22.45, -71.22) * mm, v(23.22, -70.08) * mm, v(23.5, -68.35) * mm]});
            skFitSpline(sketch, "E257", {"points": [v(23.5, -68.35) * mm, v(23.9, -65.9) * mm, v(24.16, -65.2) * mm, v(25.1, -63.87) * mm]});
            skFitSpline(sketch, "E258", {"points": [v(25.1, -63.87) * mm, v(26.18, -62.33) * mm, v(26.35, -61.85) * mm, v(26.67, -59.46) * mm]});
            skFitSpline(sketch, "E259", {"points": [v(26.67, -59.46) * mm, v(26.98, -57.13) * mm, v(27.93, -54.18) * mm, v(28.89, -52.58) * mm]});
            skFitSpline(sketch, "E260", {"points": [v(28.89, -52.58) * mm, v(29.3, -51.88) * mm, v(30.25, -50.69) * mm, v(31, -49.93) * mm]});
            skFitSpline(sketch, "E261", {"points": [v(31, -49.93) * mm, v(33.26, -47.61) * mm, v(35.36, -45.01) * mm, v(35.9, -43.88) * mm]});
            skFitSpline(sketch, "E262", {"points": [v(35.9, -43.88) * mm, v(36.17, -43.28) * mm, v(36.49, -42.11) * mm, v(36.6, -41.27) * mm]});
            skFitSpline(sketch, "E263", {"points": [v(36.6, -41.27) * mm, v(36.81, -39.5) * mm, v(37.06, -39.06) * mm, v(38.37, -38.07) * mm]});
            skFitSpline(sketch, "E264", {"points": [v(38.37, -38.07) * mm, v(39.26, -37.4) * mm, v(40.2, -36.1) * mm, v(40.2, -35.57) * mm]});
            skFitSpline(sketch, "E265", {"points": [v(40.2, -35.57) * mm, v(40.2, -35.45) * mm, v(39.98, -35.11) * mm, v(39.7, -34.83) * mm]});
            skFitSpline(sketch, "E266", {"points": [v(39.7, -34.83) * mm, v(38.98, -34.12) * mm, v(38.86, -33.18) * mm, v(39.13, -30.68) * mm]});
            skFitSpline(sketch, "E267", {"points": [v(39.13, -30.68) * mm, v(39.26, -29.5) * mm, v(39.36, -26.93) * mm, v(39.36, -24.95) * mm]});
            skFitSpline(sketch, "E268", {"points": [v(39.36, -24.95) * mm, v(39.36, -21.87) * mm, v(39.3, -21.22) * mm, v(38.94, -20.3) * mm]});
            skFitSpline(sketch, "E269", {"points": [v(38.94, -20.3) * mm, v(38.39, -18.9) * mm, v(38.4, -18.51) * mm, v(39.04, -18) * mm]});
            skFitSpline(sketch, "E270", {"points": [v(39.04, -18) * mm, v(39.45, -17.69) * mm, v(39.57, -17.4) * mm, v(39.57, -16.76) * mm]});
            skFitSpline(sketch, "E271", {"points": [v(39.57, -16.76) * mm, v(39.57, -16.2) * mm, v(39.7, -15.8) * mm, v(39.97, -15.56) * mm]});
            skFitSpline(sketch, "E272", {"points": [v(39.97, -15.56) * mm, v(40.59, -15) * mm, v(40.32, -14.37) * mm, v(39.46, -14.37) * mm]});
            skFitSpline(sketch, "E273", {"points": [v(39.46, -14.37) * mm, v(38.38, -14.37) * mm, v(37.67, -13.4) * mm, v(37.67, -11.9) * mm]});
            skFitSpline(sketch, "E274", {"points": [v(37.67, -11.9) * mm, v(37.67, -10.72) * mm, v(37.93, -9.95) * mm, v(38.44, -9.65) * mm]});
            skFitSpline(sketch, "E275", {"points": [v(38.44, -9.65) * mm, v(39.04, -9.3) * mm, v(38.7, -8.02) * mm, v(38, -8.02) * mm]});
            skFitSpline(sketch, "E276", {"points": [v(38, -8.02) * mm, v(37.74, -8.02) * mm, v(37, -7.64) * mm, v(36.34, -7.18) * mm]});
            skFitSpline(sketch, "E277", {"points": [v(36.34, -7.18) * mm, v(35.18, -6.34) * mm, v(34.43, -6.12) * mm, v(34.18, -6.54) * mm]});
            skFitSpline(sketch, "E278", {"points": [v(34.18, -6.54) * mm, v(34.1, -6.66) * mm, v(33.87, -6.75) * mm, v(33.65, -6.75) * mm]});
            skFitSpline(sketch, "E279", {"points": [v(33.65, -6.75) * mm, v(33.07, -6.75) * mm, v(30.08, -5.09) * mm, v(29.83, -4.63) * mm]});
            skFitSpline(sketch, "E280", {"points": [v(29.83, -4.63) * mm, v(29.5, -4) * mm, v(29.6, -2.89) * mm, v(30.04, -2.22) * mm]});
            skFitSpline(sketch, "E281", {"points": [v(30.04, -2.22) * mm, v(30.4, -1.66) * mm, v(30.41, -1.54) * mm, v(30.14, -1.01) * mm]});
            skFitSpline(sketch, "E282", {"points": [v(30.14, -1.01) * mm, v(29.71, -0.19) * mm, v(29.76, 0.38) * mm, v(30.37, 1.68) * mm]});
            skFitSpline(sketch, "E283", {"points": [v(30.37, 1.68) * mm, v(30.96, 2.95) * mm, v(31, 3.5) * mm, v(30.65, 4.7) * mm]});
            skFitSpline(sketch, "E284", {"points": [v(30.65, 4.7) * mm, v(30.44, 5.4) * mm, v(30.46, 5.58) * mm, v(30.78, 5.93) * mm]});
            skFitSpline(sketch, "E285", {"points": [v(30.78, 5.93) * mm, v(31.13, 6.33) * mm, v(31.13, 6.4) * mm, v(30.68, 7.79) * mm]});
            skFitSpline(sketch, "E286", {"points": [v(30.68, 7.79) * mm, v(30.01, 9.8) * mm, v(29.64, 10.47) * mm, v(28.1, 12.43) * mm]});
            skFitSpline(sketch, "E287", {"points": [v(28.1, 12.43) * mm, v(27.35, 13.37) * mm, v(26.61, 14.44) * mm, v(26.46, 14.8) * mm]});
            skFitSpline(sketch, "E288", {"points": [v(26.46, 14.8) * mm, v(26, 15.95) * mm, v(26.28, 17.5) * mm, v(27.26, 19.16) * mm]});
            skFitSpline(sketch, "E289", {"points": [v(27.26, 19.16) * mm, v(28.4, 21.1) * mm, v(28.53, 21.7) * mm, v(27.93, 22.5) * mm]});
            skFitSpline(sketch, "E290", {"points": [v(27.93, 22.5) * mm, v(27.4, 23.23) * mm, v(27.46, 23.77) * mm, v(28.28, 25.17) * mm]});
            skFitSpline(sketch, "E291", {"points": [v(28.28, 25.17) * mm, v(28.94, 26.3) * mm, v(29.89, 26.9) * mm, v(31.02, 26.9) * mm]});
            skFitSpline(sketch, "E292", {"points": [v(31.02, 26.9) * mm, v(31.6, 26.9) * mm, v(32.1, 27.06) * mm, v(32.48, 27.36) * mm]});
            skFitSpline(sketch, "E293", {"points": [v(32.48, 27.36) * mm, v(33, 27.78) * mm, v(33.05, 27.91) * mm, v(32.96, 28.95) * mm]});
            skFitSpline(sketch, "E294", {"points": [v(32.96, 28.95) * mm, v(32.91, 29.57) * mm, v(32.82, 30.13) * mm, v(32.76, 30.19) * mm]});
            skFitSpline(sketch, "E295", {"points": [v(32.76, 30.19) * mm, v(32.7, 30.25) * mm, v(32.3, 30.15) * mm, v(31.89, 29.97) * mm]});
            skFitSpline(sketch, "E296", {"points": [v(31.89, 29.97) * mm, v(31.46, 29.8) * mm, v(31.06, 29.65) * mm, v(30.98, 29.65) * mm]});
            skFitSpline(sketch, "E297", {"points": [v(30.98, 29.65) * mm, v(30.9, 29.65) * mm, v(30.9, 30.37) * mm, v(30.97, 31.24) * mm]});
            skFitSpline(sketch, "E298", {"points": [v(30.97, 31.24) * mm, v(31.1, 32.73) * mm, v(31.07, 32.83) * mm, v(30.68, 32.83) * mm]});
            skFitSpline(sketch, "E299", {"points": [v(30.68, 32.83) * mm, v(30.45, 32.83) * mm, v(30.26, 32.97) * mm, v(30.26, 33.15) * mm]});
            skFitSpline(sketch, "E300", {"points": [v(30.26, 33.15) * mm, v(30.26, 33.32) * mm, v(30.16, 33.46) * mm, v(30.05, 33.46) * mm]});
            skFitSpline(sketch, "E301", {"points": [v(30.05, 33.46) * mm, v(29.69, 33.46) * mm, v(29.82, 34.44) * mm, v(30.23, 34.81) * mm]});
            skFitSpline(sketch, "E302", {"points": [v(30.23, 34.81) * mm, v(30.44, 35) * mm, v(31.16, 35.28) * mm, v(31.83, 35.42) * mm]});
            skFitSpline(sketch, "E303", {"points": [v(31.83, 35.42) * mm, v(32.85, 35.63) * mm, v(33.13, 35.62) * mm, v(33.6, 35.36) * mm]});
            skFitSpline(sketch, "E304", {"points": [v(33.6, 35.36) * mm, v(34.37, 34.93) * mm, v(34.48, 34.05) * mm, v(33.82, 33.73) * mm]});
            skFitSpline(sketch, "E305", {"points": [v(33.82, 33.73) * mm, v(33.34, 33.51) * mm, v(33.35, 33.5) * mm, v(34.15, 33.16) * mm]});
            skFitSpline(sketch, "E306", {"points": [v(34.15, 33.16) * mm, v(34.9, 32.83) * mm, v(34.99, 32.83) * mm, v(35.36, 33.17) * mm]});
            skFitSpline(sketch, "E307", {"points": [v(35.36, 33.17) * mm, v(35.58, 33.37) * mm, v(35.76, 33.64) * mm, v(35.76, 33.77) * mm]});
            skFitSpline(sketch, "E308", {"points": [v(35.76, 33.77) * mm, v(35.76, 33.9) * mm, v(36.1, 34.7) * mm, v(36.5, 35.56) * mm]});
            skFitSpline(sketch, "E309", {"points": [v(36.5, 35.56) * mm, v(37.29, 37.18) * mm, v(37.3, 37.75) * mm, v(36.61, 38.12) * mm]});
            skFitSpline(sketch, "E310", {"points": [v(36.61, 38.12) * mm, v(36.14, 38.38) * mm, v(35.55, 38.19) * mm, v(35.55, 37.78) * mm]});
            skFitSpline(sketch, "E311", {"points": [v(35.55, 37.78) * mm, v(35.55, 36.66) * mm, v(30.79, 39.12) * mm, v(30.36, 40.45) * mm]});
            skFitSpline(sketch, "E312", {"points": [v(30.36, 40.45) * mm, v(30.3, 40.68) * mm, v(30.34, 41.05) * mm, v(30.47, 41.29) * mm]});
            skFitSpline(sketch, "E313", {"points": [v(30.47, 41.29) * mm, v(30.77, 41.86) * mm, v(31.55, 41.83) * mm, v(33.01, 41.2) * mm]});
            skFitSpline(sketch, "E314", {"points": [v(33.01, 41.2) * mm, v(34.25, 40.67) * mm, v(34.4, 40.66) * mm, v(34.2, 41.18) * mm]});
            skFitSpline(sketch, "E315", {"points": [v(34.2, 41.18) * mm, v(34.13, 41.4) * mm, v(33.81, 41.5) * mm, v(33.34, 41.5) * mm]});
            skFitSpline(sketch, "E316", {"points": [v(33.34, 41.5) * mm, v(32.48, 41.5) * mm, v(32.37, 41.83) * mm, v(32.97, 42.57) * mm]});
            skFitSpline(sketch, "E317", {"points": [v(32.97, 42.57) * mm, v(33.3, 42.96) * mm, v(33.56, 43.04) * mm, v(34.54, 43.04) * mm]});
            skFitSpline(sketch, "E318", {"points": [v(34.54, 43.04) * mm, v(36.05, 43.02) * mm, v(36.12, 43.25) * mm, v(35.4, 45.67) * mm]});
            skFitSpline(sketch, "E319", {"points": [v(35.4, 45.67) * mm, v(34.98, 47.1) * mm, v(34.9, 47.7) * mm, v(35.01, 48.62) * mm]});
            skFitSpline(sketch, "E320", {"points": [v(35.01, 48.62) * mm, v(35.1, 49.37) * mm, v(35.26, 49.76) * mm, v(35.45, 49.76) * mm]});
            skFitSpline(sketch, "E321", {"points": [v(35.45, 49.76) * mm, v(35.79, 49.76) * mm, v(36.46, 48.04) * mm, v(36.81, 46.27) * mm]});
            skFitSpline(sketch, "E322", {"points": [v(36.81, 46.27) * mm, v(37.15, 44.53) * mm, v(37.45, 43.62) * mm, v(37.68, 43.62) * mm]});
            skFitSpline(sketch, "E323", {"points": [v(37.68, 43.62) * mm, v(37.8, 43.62) * mm, v(37.88, 43.84) * mm, v(37.88, 44.1) * mm]});
            skFitSpline(sketch, "E324", {"points": [v(37.88, 44.1) * mm, v(37.88, 44.74) * mm, v(36.88, 48.83) * mm, v(36.6, 49.36) * mm]});
            skFitSpline(sketch, "E325", {"points": [v(36.6, 49.36) * mm, v(36.47, 49.6) * mm, v(36.29, 50.3) * mm, v(36.19, 50.92) * mm]});
            skFitSpline(sketch, "E326", {"points": [v(36.19, 50.92) * mm, v(36.09, 51.54) * mm, v(35.8, 52.48) * mm, v(35.57, 53.01) * mm]});
            skFitSpline(sketch, "E327", {"points": [v(35.57, 53.01) * mm, v(35.31, 53.57) * mm, v(35.13, 54.41) * mm, v(35.13, 55.03) * mm]});
            skFitSpline(sketch, "E328", {"points": [v(35.13, 55.03) * mm, v(35.13, 56.37) * mm, v(34.52, 57.14) * mm, v(33.05, 57.66) * mm]});
            skFitSpline(sketch, "E329", {"points": [v(33.05, 57.66) * mm, v(31.97, 58.05) * mm, v(31.44, 58.5) * mm, v(31.02, 59.34) * mm]});
            skFitSpline(sketch, "E330", {"points": [v(31.02, 59.34) * mm, v(30.64, 60.08) * mm, v(29.4, 60.31) * mm, v(25.6, 60.34) * mm]});
            skFitSpline(sketch, "E331", {"points": [v(25.6, 60.34) * mm, v(21.36, 60.37) * mm, v(20.2, 60.66) * mm, v(19.62, 61.83) * mm]});
            skFitSpline(sketch, "E332", {"points": [v(19.62, 61.83) * mm, v(19.42, 62.24) * mm, v(19.25, 63.05) * mm, v(19.25, 63.63) * mm]});
            skFitSpline(sketch, "E333", {"points": [v(19.25, 63.63) * mm, v(19.24, 64.97) * mm, v(18.71, 66.14) * mm, v(17.39, 67.73) * mm]});
            skFitSpline(sketch, "E334", {"points": [v(17.39, 67.73) * mm, v(15.95, 69.45) * mm, v(15.56, 70.55) * mm, v(15.72, 72.4) * mm]});
            skFitSpline(sketch, "E335", {"points": [v(15.72, 72.4) * mm, v(15.89, 74.42) * mm, v(15.61, 75.26) * mm, v(14.57, 75.97) * mm]});
            skFitSpline(sketch, "E336", {"points": [v(14.57, 75.97) * mm, v(13.8, 76.48) * mm, v(12.94, 77.13) * mm, v(10.52, 78.96) * mm]});
            skFitSpline(sketch, "E337", {"points": [v(10.52, 78.96) * mm, v(9.93, 79.4) * mm, v(9.37, 79.6) * mm, v(8.4, 79.72) * mm]});
            skFitSpline(sketch, "E338", {"points": [v(8.4, 79.72) * mm, v(7.67, 79.8) * mm, v(6.83, 80.05) * mm, v(6.52, 80.27) * mm]});
            skFitSpline(sketch, "E339", {"points": [v(6.52, 80.27) * mm, v(5.73, 80.83) * mm, v(4.99, 80.76) * mm, v(4.18, 80.06) * mm]});
            skFitSpline(sketch, "E340", {"points": [v(4.18, 80.06) * mm, v(3.06, 79.09) * mm, v(2.62, 78.93) * mm, v(1.4, 79.08) * mm]});
            skFitSpline(sketch, "E341", {"points": [v(-1.23, 77.67) * mm, v(-2.35, 76.53) * mm, v(-2.88, 75.8) * mm, v(-3.2, 74.95) * mm]});
            skFitSpline(sketch, "E342", {"points": [v(-3.2, 74.95) * mm, v(-3.44, 74.31) * mm, v(-3.84, 73.58) * mm, v(-4.08, 73.32) * mm]});
            skFitSpline(sketch, "E343", {"points": [v(-4.08, 73.32) * mm, v(-4.6, 72.75) * mm, v(-5.86, 72.28) * mm, v(-7.31, 72.1) * mm]});
            skFitSpline(sketch, "E344", {"points": [v(-7.31, 72.1) * mm, v(-8.5, 71.94) * mm, v(-9.16, 71.58) * mm, v(-9.92, 70.68) * mm]});
            skFitSpline(sketch, "E345", {"points": [v(-9.92, 70.68) * mm, v(-10.62, 69.85) * mm, v(-11.46, 69.45) * mm, v(-12.51, 69.45) * mm]});
            skFitSpline(sketch, "E346", {"points": [v(-13.27, 67.07) * mm, v(-13.12, 64.4) * mm, v(-13.35, 63.34) * mm, v(-14.15, 63) * mm]});
            skFitSpline(sketch, "E347", {"points": [v(-14.15, 63) * mm, v(-14.41, 62.88) * mm, v(-14.68, 62.54) * mm, v(-14.74, 62.25) * mm]});
            skFitSpline(sketch, "E348", {"points": [v(-14.74, 62.25) * mm, v(-14.95, 61.27) * mm, v(-15.22, 60.8) * mm, v(-15.67, 60.66) * mm]});
            skFitSpline(sketch, "E349", {"points": [v(-15.67, 60.66) * mm, v(-16.3, 60.47) * mm, v(-17.15, 61.07) * mm, v(-17.15, 61.71) * mm]});
            skFitSpline(sketch, "E350", {"points": [v(-17.15, 61.71) * mm, v(-17.15, 62.4) * mm, v(-17.57, 62.62) * mm, v(-17.95, 62.12) * mm]});
            skFitSpline(sketch, "E351", {"points": [v(-17.95, 62.12) * mm, v(-18.25, 61.72) * mm, v(-18.24, 60.86) * mm, v(-17.87, 57.55) * mm]});
            skFitSpline(sketch, "E352", {"points": [v(-17.87, 57.55) * mm, v(-17.76, 56.53) * mm, v(-17.83, 56.11) * mm, v(-18.31, 54.9) * mm]});
            skFitSpline(sketch, "E353", {"points": [v(-18.43, 53.1) * mm, v(-18.09, 52.84) * mm, v(-18, 52.61) * mm, v(-18.12, 52.26) * mm]});
            skFitSpline(sketch, "E354", {"points": [v(-18.12, 52.26) * mm, v(-18.35, 51.5) * mm, v(-18.6, 51.29) * mm, v(-19.44, 51.14) * mm]});
            skFitSpline(sketch, "E355", {"points": [v(-19.44, 51.14) * mm, v(-20.16, 51.02) * mm, v(-20.25, 50.92) * mm, v(-20.59, 49.92) * mm]});
            skFitSpline(sketch, "E356", {"points": [v(-20.59, 49.92) * mm, v(-21.07, 48.49) * mm, v(-20.79, 47.82) * mm, v(-19.64, 47.63) * mm]});
            skFitSpline(sketch, "E357", {"points": [v(-19.64, 47.63) * mm, v(-18.7, 47.48) * mm, v(-18.1, 46.98) * mm, v(-17.9, 46.22) * mm]});
            skFitSpline(sketch, "E358", {"points": [v(-17.9, 46.22) * mm, v(-17.82, 45.92) * mm, v(-17.92, 44.77) * mm, v(-18.12, 43.68) * mm]});
            skFitSpline(sketch, "E359", {"points": [v(-18.12, 43.68) * mm, v(-18.44, 41.9) * mm, v(-18.54, 41.66) * mm, v(-19.03, 41.44) * mm]});
            skFitSpline(sketch, "E360", {"points": [v(-19.03, 41.44) * mm, v(-19.33, 41.3) * mm, v(-19.75, 41.02) * mm, v(-19.96, 40.82) * mm]});
            skFitSpline(sketch, "E361", {"points": [v(-19.96, 40.82) * mm, v(-20.16, 40.62) * mm, v(-20.6, 40.45) * mm, v(-20.94, 40.45) * mm]});
            skFitSpline(sketch, "E362", {"points": [v(-21.44, 41.8) * mm, v(-21.32, 43.27) * mm, v(-21.6, 44.43) * mm, v(-22.21, 44.98) * mm]});
            skFitSpline(sketch, "E363", {"points": [v(-22.21, 44.98) * mm, v(-22.54, 45.28) * mm, v(-22.7, 45.3) * mm, v(-23.16, 45.08) * mm]});
            skFitSpline(sketch, "E364", {"points": [v(-23.16, 45.08) * mm, v(-23.48, 44.93) * mm, v(-23.72, 44.65) * mm, v(-23.72, 44.41) * mm]});
            skFitSpline(sketch, "E365", {"points": [v(-23.72, 44.41) * mm, v(-23.72, 44.19) * mm, v(-24.06, 43.69) * mm, v(-24.47, 43.3) * mm]});
            skFitSpline(sketch, "E366", {"points": [v(-24.8, 41.05) * mm, v(-24.28, 39.2) * mm, v(-24.4, 38.43) * mm, v(-25.38, 37) * mm]});
            skFitSpline(sketch, "E367", {"points": [v(-25.38, 37) * mm, v(-26.38, 35.55) * mm, v(-26.52, 35.03) * mm, v(-26.15, 34.3) * mm]});
            skFitSpline(sketch, "E368", {"points": [v(-26.15, 34.3) * mm, v(-25.74, 33.52) * mm, v(-25.75, 32.64) * mm, v(-26.17, 31.34) * mm]});
            skFitSpline(sketch, "E369", {"points": [v(-26.17, 31.34) * mm, v(-26.5, 30.34) * mm, v(-26.5, 30.27) * mm, v(-26.05, 29.35) * mm]});
            skFitSpline(sketch, "E370", {"points": [v(-26.05, 29.35) * mm, v(-25.45, 28.12) * mm, v(-24.64, 27.64) * mm, v(-22.5, 27.27) * mm]});
            skFitSpline(sketch, "E371", {"points": [v(-22.5, 27.27) * mm, v(-21.03, 27.01) * mm, v(-20.71, 27.01) * mm, v(-20.51, 27.25) * mm]});
            skFitSpline(sketch, "E372", {"points": [v(-20.51, 27.25) * mm, v(-20.2, 27.62) * mm, v(-19.6, 27.62) * mm, v(-19.29, 27.24) * mm]});
            skFitSpline(sketch, "E373", {"points": [v(-19.29, 27.24) * mm, v(-18.74, 26.58) * mm, v(-18.77, 25.45) * mm, v(-19.37, 23.93) * mm]});
            skFitSpline(sketch, "E374", {"points": [v(-19.37, 23.93) * mm, v(-19.7, 23.08) * mm, v(-20.07, 22.46) * mm, v(-20.24, 22.46) * mm]});
            skFitSpline(sketch, "E375", {"points": [v(-20.24, 22.46) * mm, v(-20.4, 22.46) * mm, v(-20.54, 22.54) * mm, v(-20.54, 22.65) * mm]});
            skFitSpline(sketch, "E376", {"points": [v(-20.54, 22.65) * mm, v(-20.54, 23.08) * mm, v(-22.27, 25) * mm, v(-22.65, 25) * mm]});
            skFitSpline(sketch, "E377", {"points": [v(-22.65, 25) * mm, v(-23.23, 25) * mm, v(-23.72, 24.2) * mm, v(-23.72, 23.22) * mm]});
            skFitSpline(sketch, "E378", {"points": [v(-23.72, 23.22) * mm, v(-23.72, 22.72) * mm, v(-23.92, 22.04) * mm, v(-24.24, 21.5) * mm]});
            skFitSpline(sketch, "E379", {"points": [v(-24.24, 21.5) * mm, v(-24.66, 20.79) * mm, v(-24.75, 20.34) * mm, v(-24.74, 19.26) * mm]});
            skFitSpline(sketch, "E380", {"points": [v(-24.74, 19.26) * mm, v(-24.72, 18.51) * mm, v(-24.78, 17.69) * mm, v(-24.86, 17.43) * mm]});
            skFitSpline(sketch, "E381", {"points": [v(-24.86, 17.43) * mm, v(-25.08, 16.75) * mm, v(-24.82, 16.1) * mm, v(-24.33, 16.1) * mm]});
            skFitSpline(sketch, "E382", {"points": [v(-24.33, 16.1) * mm, v(-23.36, 16.1) * mm, v(-23.83, 14.55) * mm, v(-24.88, 14.3) * mm]});
            skFitSpline(sketch, "E383", {"points": [v(-24.88, 14.3) * mm, v(-25.3, 14.18) * mm, v(-25.36, 14.09) * mm, v(-25.2, 13.77) * mm]});
            skFitSpline(sketch, "E384", {"points": [v(-25.2, 13.77) * mm, v(-24.96, 13.34) * mm, v(-24.91, 12.23) * mm, v(-25.11, 12.03) * mm]});
            skFitSpline(sketch, "E385", {"points": [v(-25.11, 12.03) * mm, v(-25.18, 11.96) * mm, v(-25.46, 11.98) * mm, v(-25.73, 12.09) * mm]});
            skFitSpline(sketch, "E386", {"points": [v(-25.73, 12.09) * mm, v(-26.03, 12.2) * mm, v(-26.5, 12.18) * mm, v(-26.98, 12.04) * mm]});
            skFitSpline(sketch, "E387", {"points": [v(-26.98, 12.04) * mm, v(-28.78, 11.48) * mm, v(-28.79, 13.48) * mm, v(-26.99, 14.98) * mm]});
            skFitSpline(sketch, "E388", {"points": [v(-26.99, 14.98) * mm, v(-26.47, 15.42) * mm, v(-26.04, 15.92) * mm, v(-26.04, 16.09) * mm]});
            skFitSpline(sketch, "E389", {"points": [v(-26.04, 16.09) * mm, v(-26.04, 16.33) * mm, v(-26.1, 16.35) * mm, v(-26.3, 16.15) * mm]});
            skFitSpline(sketch, "E390", {"points": [v(-26.3, 16.15) * mm, v(-26.76, 15.69) * mm, v(-27.73, 15.86) * mm, v(-28.39, 16.52) * mm]});
            skFitSpline(sketch, "E391", {"points": [v(-28.39, 16.52) * mm, v(-28.98, 17.1) * mm, v(-29, 17.22) * mm, v(-29, 18.97) * mm]});
            skFitSpline(sketch, "E392", {"points": [v(-29, 18.97) * mm, v(-29, 20.63) * mm, v(-29.05, 20.82) * mm, v(-29.43, 20.91) * mm]});
            skFitSpline(sketch, "E393", {"points": [v(-29.43, 20.91) * mm, v(-30.19, 21.11) * mm, v(-29.94, 22.23) * mm, v(-28.69, 24.26) * mm]});
            skFitSpline(sketch, "E394", {"points": [v(-28.69, 24.26) * mm, v(-27.87, 25.58) * mm, v(-28, 27.33) * mm, v(-28.9, 27.33) * mm]});
            skFitSpline(sketch, "E395", {"points": [v(-28.9, 27.33) * mm, v(-29.17, 27.33) * mm, v(-29.7, 27.61) * mm, v(-30.07, 27.96) * mm]});
            skFitSpline(sketch, "E396", {"points": [v(-30.07, 27.96) * mm, v(-30.87, 28.71) * mm, v(-31.12, 28.76) * mm, v(-31.12, 28.14) * mm]});
            skFitSpline(sketch, "E397", {"points": [v(-31.12, 28.14) * mm, v(-31.12, 27.9) * mm, v(-30.7, 27.23) * mm, v(-30.17, 26.67) * mm]});
            skFitSpline(sketch, "E398", {"points": [v(-30.17, 26.67) * mm, v(-29.12, 25.55) * mm, v(-29.07, 25.4) * mm, v(-29.55, 24.9) * mm]});
            skFitSpline(sketch, "E399", {"points": [v(-29.55, 24.9) * mm, v(-30.1, 24.36) * mm, v(-30.96, 24.5) * mm, v(-31.6, 25.23) * mm]});
            skFitSpline(sketch, "E400", {"points": [v(-31.6, 25.23) * mm, v(-32.15, 25.85) * mm, v(-32.25, 25.88) * mm, v(-33.19, 25.74) * mm]});
            skFitSpline(sketch, "E401", {"points": [v(-33.19, 25.74) * mm, v(-34.37, 25.57) * mm, v(-35.26, 25.15) * mm, v(-35.43, 24.68) * mm]});
            skFitSpline(sketch, "E402", {"points": [v(-35.43, 24.68) * mm, v(-35.6, 24.23) * mm, v(-35.14, 24.08) * mm, v(-34.43, 24.35) * mm]});
            skFitSpline(sketch, "E403", {"points": [v(-34.43, 24.35) * mm, v(-34.1, 24.48) * mm, v(-33.54, 24.57) * mm, v(-33.15, 24.57) * mm]});
            skFitSpline(sketch, "E404", {"points": [v(-33.15, 24.57) * mm, v(-32.54, 24.57) * mm, v(-32.46, 24.5) * mm, v(-32.44, 24) * mm]});
            skFitSpline(sketch, "E405", {"points": [v(-32.44, 24) * mm, v(-32.43, 23.67) * mm, v(-32.27, 23.06) * mm, v(-32.1, 22.62) * mm]});
            skFitSpline(sketch, "E406", {"points": [v(-32.1, 22.62) * mm, v(-31.58, 21.42) * mm, v(-31.67, 20.28) * mm, v(-32.4, 18.86) * mm]});
            skFitSpline(sketch, "E407", {"points": [v(-32.4, 18.86) * mm, v(-33.14, 17.4) * mm, v(-33.17, 17.05) * mm, v(-32.63, 16.75) * mm]});
            skFitSpline(sketch, "E408", {"points": [v(-32.63, 16.75) * mm, v(-32.1, 16.47) * mm, v(-31.55, 14.82) * mm, v(-31.55, 13.54) * mm]});
            skFitSpline(sketch, "E409", {"points": [v(-31.55, 13.54) * mm, v(-31.55, 12.77) * mm, v(-31.45, 12.46) * mm, v(-31.11, 12.23) * mm]});
            skFitSpline(sketch, "E410", {"points": [v(-31.11, 12.23) * mm, v(-30.88, 12.06) * mm, v(-30.63, 11.6) * mm, v(-30.56, 11.18) * mm]});
            skFitSpline(sketch, "E411", {"points": [v(-30.56, 11.18) * mm, v(-30.46, 10.56) * mm, v(-30.52, 10.4) * mm, v(-30.91, 10.18) * mm]});
            skFitSpline(sketch, "E412", {"points": [v(-30.91, 10.18) * mm, v(-31.53, 9.85) * mm, v(-32.75, 10.1) * mm, v(-33.03, 10.6) * mm]});
            skFitSpline(sketch, "E413", {"points": [v(-33.03, 10.6) * mm, v(-33.14, 10.82) * mm, v(-33.25, 11.41) * mm, v(-33.26, 11.91) * mm]});
            skFitSpline(sketch, "E414", {"points": [v(-33.26, 11.91) * mm, v(-33.27, 12.53) * mm, v(-33.55, 13.4) * mm, v(-34.16, 14.63) * mm]});
            skFitSpline(sketch, "E415", {"points": [v(-34.16, 14.63) * mm, v(-34.97, 16.28) * mm, v(-35.1, 16.43) * mm, v(-35.72, 16.5) * mm]});
            skFitSpline(sketch, "E416", {"points": [v(-35.72, 16.5) * mm, v(-36.31, 16.55) * mm, v(-36.58, 16.38) * mm, v(-37.73, 15.23) * mm]});
            skFitSpline(sketch, "E417", {"points": [v(-37.73, 15.23) * mm, v(-38.93, 14.04) * mm, v(-39.01, 13.9) * mm, v(-38.59, 13.83) * mm]});
            skFitSpline(sketch, "E418", {"points": [v(-38.59, 13.83) * mm, v(-38.17, 13.76) * mm, v(-38.1, 13.62) * mm, v(-38.11, 12.76) * mm]});
            skFitSpline(sketch, "E419", {"points": [v(-38.11, 12.76) * mm, v(-38.12, 12.21) * mm, v(-38.4, 10.97) * mm, v(-38.75, 9.98) * mm]});
            skFitSpline(sketch, "E420", {"points": [v(-38.75, 9.98) * mm, v(-39.51, 7.8) * mm, v(-39.52, 7.37) * mm, v(-38.83, 5.2) * mm]});
            skFitSpline(sketch, "E421", {"points": [v(-38.83, 5.2) * mm, v(-38.38, 3.8) * mm, v(-38.3, 3.15) * mm, v(-38.32, 1.4) * mm]});
            skFitSpline(sketch, "E422", {"points": [v(-38.32, 1.4) * mm, v(-38.34, 0.23) * mm, v(-38.26, -1.1) * mm, v(-38.13, -1.57) * mm]});
            skFitSpline(sketch, "E423", {"points": [v(-38.13, -1.57) * mm, v(-37.77, -2.92) * mm, v(-37.86, -6.07) * mm, v(-38.34, -8.88) * mm]});
            skFitSpline(sketch, "E424", {"points": [v(-38.34, -8.88) * mm, v(-38.63, -10.58) * mm, v(-38.76, -12.12) * mm, v(-38.71, -13.3) * mm]});
            skFitSpline(sketch, "E425", {"points": [v(-38.71, -13.3) * mm, v(-38.65, -14.92) * mm, v(-38.56, -15.24) * mm, v(-37.96, -16.18) * mm]});
            skFitSpline(sketch, "E426", {"points": [v(-37.41, -20.41) * mm, v(-37.55, -24.06) * mm, v(-37.43, -24.65) * mm, v(-36.22, -26.18) * mm]});
            skFitSpline(sketch, "E427", {"points": [v(-36.22, -26.18) * mm, v(-34.5, -28.36) * mm, v(-33.66, -30.2) * mm, v(-33.66, -31.8) * mm]});
            skFitSpline(sketch, "E428", {"points": [v(-33.66, -31.8) * mm, v(-33.66, -32.5) * mm, v(-33.82, -32.8) * mm, v(-34.62, -33.66) * mm]});
            skFitSpline(sketch, "E429", {"points": [v(-34.62, -33.66) * mm, v(-35.46, -34.56) * mm, v(-35.57, -34.79) * mm, v(-35.57, -35.64) * mm]});
            skFitSpline(sketch, "E430", {"points": [v(-35.57, -35.64) * mm, v(-35.57, -36.85) * mm, v(-35.16, -37.86) * mm, v(-34.2, -38.96) * mm]});
            skFitSpline(sketch, "E431", {"points": [v(-34.2, -38.96) * mm, v(-33.8, -39.44) * mm, v(-33.28, -40.4) * mm, v(-33.04, -41.1) * mm]});
            skFitSpline(sketch, "E432", {"points": [v(-33.04, -41.1) * mm, v(-32.76, -41.93) * mm, v(-32.24, -42.8) * mm, v(-31.56, -43.59) * mm]});
            skFitSpline(sketch, "E433", {"points": [v(-31.56, -43.59) * mm, v(-29.64, -45.8) * mm, v(-29.61, -45.88) * mm, v(-29.6, -49.55) * mm]});
            skFitSpline(sketch, "E434", {"points": [v(-29.6, -49.55) * mm, v(-29.59, -51.33) * mm, v(-29.65, -53.1) * mm, v(-29.74, -53.47) * mm]});
            skFitSpline(sketch, "E435", {"points": [v(-29.74, -53.47) * mm, v(-29.87, -54.05) * mm, v(-29.78, -54.34) * mm, v(-29.2, -55.24) * mm]});
            skFitSpline(sketch, "E436", {"points": [v(-29.2, -55.24) * mm, v(-28.02, -57.1) * mm, v(-28.34, -58.63) * mm, v(-30.4, -60.92) * mm]});
            skFitSpline(sketch, "E437", {"points": [v(-30.9, -63.02) * mm, v(-30.62, -63.56) * mm, v(-29.54, -65.09) * mm, v(-28.5, -66.4) * mm]});
            skFitSpline(sketch, "E438", {"points": [v(-28.5, -66.4) * mm, v(-27.47, -67.73) * mm, v(-25.87, -70.02) * mm, v(-24.93, -71.5) * mm]});
            skFitSpline(sketch, "E439", {"points": [v(-24.93, -71.5) * mm, v(-21.66, -76.64) * mm, v(-20.53, -77.82) * mm, v(-18.3, -78.38) * mm]});
            skFitSpline(sketch, "E440", {"points": [v(-18.3, -78.38) * mm, v(-17.5, -78.58) * mm, v(-15.88, -79.13) * mm, v(-14.72, -79.6) * mm]});
            skFitSpline(sketch, "E441", {"points": [v(-14.72, -79.6) * mm, v(-13.56, -80.07) * mm, v(-12.22, -80.53) * mm, v(-11.76, -80.63) * mm]});
            skFitSpline(sketch, "E442", {"points": [v(-11.76, -80.63) * mm, v(-10.67, -80.86) * mm, v(-8.14, -80.7) * mm, v(-6.84, -80.3) * mm]});
            skFitSpline(sketch, "E443", {"points": [v(-34.5, 19.17) * mm, v(-34.65, 19.34) * mm, v(-35.11, 19.55) * mm, v(-35.54, 19.62) * mm]});
            skFitSpline(sketch, "E444", {"points": [v(-35.54, 19.62) * mm, v(-35.99, 19.7) * mm, v(-36.79, 20.15) * mm, v(-37.44, 20.68) * mm]});
            skFitSpline(sketch, "E445", {"points": [v(-37.44, 20.68) * mm, v(-38.07, 21.2) * mm, v(-38.96, 21.72) * mm, v(-39.42, 21.86) * mm]});
            skFitSpline(sketch, "E446", {"points": [v(-39.42, 21.86) * mm, v(-39.89, 22) * mm, v(-40.41, 22.34) * mm, v(-40.6, 22.6) * mm]});
            skFitSpline(sketch, "E447", {"points": [v(-40.6, 22.6) * mm, v(-40.88, 23.06) * mm, v(-40.88, 23.2) * mm, v(-40.52, 24.1) * mm]});
            skFitSpline(sketch, "E448", {"points": [v(-40.52, 24.1) * mm, v(-39.98, 25.46) * mm, v(-39.97, 28.27) * mm, v(-40.5, 29.07) * mm]});
            skFitSpline(sketch, "E449", {"points": [v(-40.5, 29.07) * mm, v(-40.94, 29.76) * mm, v(-40.96, 30.33) * mm, v(-40.55, 31.12) * mm]});
            skFitSpline(sketch, "E450", {"points": [v(-40.55, 31.12) * mm, v(-40.35, 31.5) * mm, v(-40.29, 32) * mm, v(-40.37, 32.52) * mm]});
            skFitSpline(sketch, "E451", {"points": [v(-40.37, 32.52) * mm, v(-40.49, 33.2) * mm, v(-40.43, 33.39) * mm, v(-39.97, 33.76) * mm]});
            skFitSpline(sketch, "E452", {"points": [v(-39.97, 33.76) * mm, v(-39.45, 34.2) * mm, v(-38.12, 36.16) * mm, v(-37.84, 36.9) * mm]});
            skFitSpline(sketch, "E453", {"points": [v(-37.84, 36.9) * mm, v(-37.74, 37.17) * mm, v(-37.47, 37.27) * mm, v(-36.87, 37.27) * mm]});
            skFitSpline(sketch, "E454", {"points": [v(-36.87, 37.27) * mm, v(-36.4, 37.27) * mm, v(-35.93, 37.4) * mm, v(-35.78, 37.6) * mm]});
            skFitSpline(sketch, "E455", {"points": [v(-35.78, 37.6) * mm, v(-35.64, 37.77) * mm, v(-35.2, 37.9) * mm, v(-34.82, 37.9) * mm]});
            skFitSpline(sketch, "E456", {"points": [v(-34.82, 37.9) * mm, v(-34.13, 37.9) * mm, v(-34.12, 37.9) * mm, v(-34.23, 37.12) * mm]});
            skFitSpline(sketch, "E457", {"points": [v(-34.23, 37.12) * mm, v(-34.47, 35.46) * mm, v(-34.75, 34.75) * mm, v(-35.37, 34.23) * mm]});
            skFitSpline(sketch, "E458", {"points": [v(-35.37, 34.23) * mm, v(-35.99, 33.7) * mm, v(-36, 33.67) * mm, v(-35.67, 33.16) * mm]});
            skFitSpline(sketch, "E459", {"points": [v(-35.67, 33.16) * mm, v(-34.87, 31.95) * mm, v(-36.1, 31.14) * mm, v(-37.5, 31.95) * mm]});
            skFitSpline(sketch, "E460", {"points": [v(-37.5, 31.95) * mm, v(-37.94, 32.2) * mm, v(-38.35, 32.4) * mm, v(-38.4, 32.4) * mm]});
            skFitSpline(sketch, "E461", {"points": [v(-38.4, 32.4) * mm, v(-38.63, 32.4) * mm, v(-38.23, 31.65) * mm, v(-37.44, 30.52) * mm]});
            skFitSpline(sketch, "E462", {"points": [v(-37.44, 30.52) * mm, v(-36.44, 29.1) * mm, v(-36.35, 28.09) * mm, v(-37.16, 27.33) * mm]});
            skFitSpline(sketch, "E463", {"points": [v(-37.16, 27.33) * mm, v(-37.75, 26.77) * mm, v(-37.88, 25.84) * mm, v(-37.36, 25.84) * mm]});
            skFitSpline(sketch, "E464", {"points": [v(-37.36, 25.84) * mm, v(-37.12, 25.84) * mm, v(-37.08, 25.7) * mm, v(-37.18, 25.26) * mm]});
            skFitSpline(sketch, "E465", {"points": [v(-37.18, 25.26) * mm, v(-37.37, 24.47) * mm, v(-37.66, 23.94) * mm, v(-37.9, 23.94) * mm]});
            skFitSpline(sketch, "E466", {"points": [v(-37.9, 23.94) * mm, v(-38.25, 23.94) * mm, v(-38.13, 23.18) * mm, v(-37.73, 22.82) * mm]});
            skFitSpline(sketch, "E467", {"points": [v(-37.73, 22.82) * mm, v(-37.52, 22.63) * mm, v(-36.88, 22.27) * mm, v(-36.3, 22.02) * mm]});
            skFitSpline(sketch, "E468", {"points": [v(-36.3, 22.02) * mm, v(-33.61, 20.87) * mm, v(-33.45, 20.76) * mm, v(-33.45, 20.13) * mm]});
            skFitSpline(sketch, "E469", {"points": [v(-33.45, 20.13) * mm, v(-33.45, 18.94) * mm, v(-33.94, 18.5) * mm, v(-34.5, 19.17) * mm]});
            skFitSpline(sketch, "E470", {"points": [v(-33.88, 20.11) * mm, v(-33.88, 20.2) * mm, v(-34.7, 20.65) * mm, v(-35.7, 21.1) * mm]});
            skFitSpline(sketch, "E471", {"points": [v(-35.7, 21.1) * mm, v(-38.2, 22.21) * mm, v(-38.53, 22.5) * mm, v(-38.53, 23.53) * mm]});
            skFitSpline(sketch, "E472", {"points": [v(-38.53, 23.53) * mm, v(-38.53, 23.99) * mm, v(-38.45, 24.36) * mm, v(-38.35, 24.36) * mm]});
            skFitSpline(sketch, "E473", {"points": [v(-38.35, 24.36) * mm, v(-38.26, 24.36) * mm, v(-38.08, 24.58) * mm, v(-37.96, 24.84) * mm]});
            skFitSpline(sketch, "E474", {"points": [v(-37.96, 24.84) * mm, v(-37.8, 25.2) * mm, v(-37.81, 25.39) * mm, v(-38.03, 25.6) * mm]});
            skFitSpline(sketch, "E475", {"points": [v(-38.03, 25.6) * mm, v(-38.5, 26.03) * mm, v(-38.36, 26.84) * mm, v(-37.67, 27.63) * mm]});
            skFitSpline(sketch, "E476", {"points": [v(-37.67, 27.63) * mm, v(-36.9, 28.51) * mm, v(-36.94, 28.8) * mm, v(-38.14, 30.48) * mm]});
            skFitSpline(sketch, "E477", {"points": [v(-38.14, 30.48) * mm, v(-38.63, 31.17) * mm, v(-38.96, 31.87) * mm, v(-38.96, 32.23) * mm]});
            skFitSpline(sketch, "E478", {"points": [v(-38.96, 32.23) * mm, v(-38.96, 32.75) * mm, v(-38.87, 32.83) * mm, v(-38.36, 32.83) * mm]});
            skFitSpline(sketch, "E479", {"points": [v(-38.36, 32.83) * mm, v(-38.03, 32.83) * mm, v(-37.58, 32.69) * mm, v(-37.36, 32.52) * mm]});
            skFitSpline(sketch, "E480", {"points": [v(-37.36, 32.52) * mm, v(-36.98, 32.23) * mm, v(-36, 32.07) * mm, v(-36, 32.3) * mm]});
            skFitSpline(sketch, "E481", {"points": [v(-36, 32.3) * mm, v(-36, 32.35) * mm, v(-36.15, 32.73) * mm, v(-36.35, 33.14) * mm]});
            skFitSpline(sketch, "E482", {"points": [v(-35.92, 34.57) * mm, v(-35.27, 35.14) * mm, v(-35.1, 35.46) * mm, v(-34.96, 36.38) * mm]});
            skFitSpline(sketch, "E483", {"points": [v(-34.96, 36.38) * mm, v(-34.86, 36.99) * mm, v(-34.82, 37.49) * mm, v(-34.87, 37.49) * mm]});
            skFitSpline(sketch, "E484", {"points": [v(-34.87, 37.49) * mm, v(-34.91, 37.49) * mm, v(-35.23, 37.28) * mm, v(-35.56, 37.04) * mm]});
            skFitSpline(sketch, "E485", {"points": [v(-35.56, 37.04) * mm, v(-35.96, 36.74) * mm, v(-36.36, 36.62) * mm, v(-36.72, 36.69) * mm]});
            skFitSpline(sketch, "E486", {"points": [v(-36.72, 36.69) * mm, v(-37.02, 36.75) * mm, v(-37.26, 36.72) * mm, v(-37.26, 36.64) * mm]});
            skFitSpline(sketch, "E487", {"points": [v(-37.26, 36.64) * mm, v(-37.26, 36.35) * mm, v(-39.4, 33.25) * mm, v(-39.6, 33.25) * mm]});
            skFitSpline(sketch, "E488", {"points": [v(-39.6, 33.25) * mm, v(-39.71, 33.25) * mm, v(-39.8, 32.75) * mm, v(-39.8, 32.14) * mm]});
            skFitSpline(sketch, "E489", {"points": [v(-39.8, 32.14) * mm, v(-39.81, 31.5) * mm, v(-39.95, 30.86) * mm, v(-40.13, 30.62) * mm]});
            skFitSpline(sketch, "E490", {"points": [v(-40.13, 30.62) * mm, v(-40.4, 30.26) * mm, v(-40.4, 30.15) * mm, v(-40.08, 29.67) * mm]});
            skFitSpline(sketch, "E491", {"points": [v(-40.08, 29.67) * mm, v(-39.54, 28.86) * mm, v(-39.43, 25.58) * mm, v(-39.9, 24.18) * mm]});
            skFitSpline(sketch, "E492", {"points": [v(-39.9, 24.18) * mm, v(-40.1, 23.59) * mm, v(-40.2, 23.02) * mm, v(-40.14, 22.92) * mm]});
            skFitSpline(sketch, "E493", {"points": [v(-40.14, 22.92) * mm, v(-40.08, 22.82) * mm, v(-39.57, 22.56) * mm, v(-39.02, 22.35) * mm]});
            skFitSpline(sketch, "E494", {"points": [v(-39.02, 22.35) * mm, v(-38.46, 22.15) * mm, v(-37.5, 21.56) * mm, v(-36.87, 21.05) * mm]});
            skFitSpline(sketch, "E495", {"points": [v(-36.87, 21.05) * mm, v(-36.12, 20.45) * mm, v(-35.53, 20.13) * mm, v(-35.13, 20.13) * mm]});
            skFitSpline(sketch, "E496", {"points": [v(-35.13, 20.13) * mm, v(-34.8, 20.13) * mm, v(-34.48, 20.03) * mm, v(-34.4, 19.91) * mm]});
            skFitSpline(sketch, "E497", {"points": [v(-34.4, 19.91) * mm, v(-34.26, 19.68) * mm, v(-33.88, 19.83) * mm, v(-33.88, 20.11) * mm]});
            skFitSpline(sketch, "E498", {"points": [v(-35.84, 27.25) * mm, v(-35.9, 27.35) * mm, v(-36.01, 27.96) * mm, v(-36.1, 28.6) * mm]});
            skFitSpline(sketch, "E499", {"points": [v(-36.1, 28.6) * mm, v(-36.27, 30.1) * mm, v(-35.9, 30.72) * mm, v(-35.07, 30.34) * mm]});
            skFitSpline(sketch, "E500", {"points": [v(-35.07, 30.34) * mm, v(-34.7, 30.18) * mm, v(-34.56, 29.98) * mm, v(-34.64, 29.77) * mm]});
            skFitSpline(sketch, "E501", {"points": [v(-34.64, 29.77) * mm, v(-34.74, 29.52) * mm, v(-34.61, 29.44) * mm, v(-34.1, 29.44) * mm]});
            skFitSpline(sketch, "E502", {"points": [v(-34.1, 29.44) * mm, v(-33.14, 29.44) * mm, v(-32.6, 29.1) * mm, v(-32.6, 28.48) * mm]});
            skFitSpline(sketch, "E503", {"points": [v(-32.6, 28.48) * mm, v(-32.6, 28.2) * mm, v(-32.71, 27.96) * mm, v(-32.85, 27.96) * mm]});
            skFitSpline(sketch, "E504", {"points": [v(-32.85, 27.96) * mm, v(-32.98, 27.96) * mm, v(-33.2, 27.8) * mm, v(-33.34, 27.62) * mm]});
            skFitSpline(sketch, "E505", {"points": [v(-33.34, 27.62) * mm, v(-33.62, 27.24) * mm, v(-35.65, 26.94) * mm, v(-35.84, 27.25) * mm]});
            skFitSpline(sketch, "E506", {"points": [v(-33.88, 28.07) * mm, v(-33.88, 28.24) * mm, v(-33.73, 28.38) * mm, v(-33.56, 28.38) * mm]});
            skFitSpline(sketch, "E507", {"points": [v(-33.56, 28.38) * mm, v(-33.38, 28.38) * mm, v(-33.24, 28.48) * mm, v(-33.24, 28.6) * mm]});
            skFitSpline(sketch, "E508", {"points": [v(-33.24, 28.6) * mm, v(-33.24, 28.71) * mm, v(-33.73, 28.8) * mm, v(-34.32, 28.8) * mm]});
            skFitSpline(sketch, "E509", {"points": [v(-34.32, 28.8) * mm, v(-35.4, 28.8) * mm, v(-35.4, 28.81) * mm, v(-35.31, 29.43) * mm]});
            skFitSpline(sketch, "E510", {"points": [v(-35.31, 29.43) * mm, v(-35.26, 29.77) * mm, v(-35.3, 30) * mm, v(-35.4, 29.95) * mm]});
            skFitSpline(sketch, "E511", {"points": [v(-35.4, 29.95) * mm, v(-35.6, 29.82) * mm, v(-35.62, 28.91) * mm, v(-35.44, 28.23) * mm]});
            skFitSpline(sketch, "E512", {"points": [v(-35.44, 28.23) * mm, v(-35.33, 27.85) * mm, v(-35.16, 27.75) * mm, v(-34.6, 27.75) * mm]});
            skFitSpline(sketch, "E513", {"points": [v(-34.6, 27.75) * mm, v(-34.1, 27.75) * mm, v(-33.88, 27.85) * mm, v(-33.88, 28.07) * mm]});
            skFitSpline(sketch, "E514", {"points": [v(-34.5, 30.49) * mm, v(-34.87, 31.18) * mm, v(-34.75, 31.97) * mm, v(-34.2, 32.53) * mm]});
            skFitSpline(sketch, "E515", {"points": [v(-34.2, 32.53) * mm, v(-33.9, 32.82) * mm, v(-33.66, 33.2) * mm, v(-33.66, 33.37) * mm]});
            skFitSpline(sketch, "E516", {"points": [v(-33.66, 33.37) * mm, v(-33.66, 33.54) * mm, v(-33.57, 33.68) * mm, v(-33.45, 33.68) * mm]});
            skFitSpline(sketch, "E517", {"points": [v(-33.45, 33.68) * mm, v(-33.34, 33.68) * mm, v(-33.24, 33.6) * mm, v(-33.24, 33.51) * mm]});
            skFitSpline(sketch, "E518", {"points": [v(-33.24, 33.51) * mm, v(-33.24, 33.42) * mm, v(-32.95, 33.24) * mm, v(-32.6, 33.1) * mm]});
            skFitSpline(sketch, "E519", {"points": [v(-32.6, 33.1) * mm, v(-31.72, 32.77) * mm, v(-31.8, 32.27) * mm, v(-32.94, 31.08) * mm]});
            skFitSpline(sketch, "E520", {"points": [v(-32.94, 31.08) * mm, v(-34, 29.96) * mm, v(-34.19, 29.9) * mm, v(-34.5, 30.49) * mm]});
            skFitSpline(sketch, "E521", {"points": [v(-32.6, 32.45) * mm, v(-32.6, 32.54) * mm, v(-32.75, 32.62) * mm, v(-32.92, 32.62) * mm]});
            skFitSpline(sketch, "E522", {"points": [v(-32.92, 32.62) * mm, v(-33.1, 32.62) * mm, v(-33.24, 32.53) * mm, v(-33.24, 32.43) * mm]});
            skFitSpline(sketch, "E523", {"points": [v(-33.24, 32.43) * mm, v(-33.24, 32.33) * mm, v(-33.43, 32.2) * mm, v(-33.66, 32.13) * mm]});
            skFitSpline(sketch, "E524", {"points": [v(-33.66, 32.13) * mm, v(-33.96, 32.06) * mm, v(-34.09, 31.84) * mm, v(-34.09, 31.43) * mm]});
            skFitSpline(sketch, "E525", {"points": [v(-33.35, 31.56) * mm, v(-32.94, 31.95) * mm, v(-32.6, 32.35) * mm, v(-32.6, 32.45) * mm]});
            skSolve(sketch);
        }
        {
            var Q0;
            Q0=makeQuery(id+"F0.imprint","IMPRINT",FACE,{"disambiguationData":[TD([[makeQuery(id+"F0.imprint","IMPRINT",EDGE,{"derivedFrom":sQuery(id+"F0.wireOp",EDGE,"E12")}),1.0]])]});
            var Q1;
            Q1=makeQuery(id+"F0.imprint","IMPRINT",FACE,{"disambiguationData":[TD([[makeQuery(id+"F0.imprint","IMPRINT",EDGE,{"derivedFrom":sQuery(id+"F0.wireOp",EDGE,"E26")}),1.0]])]});
            var Q2;
            Q2=makeQuery(id+"F0.imprint","IMPRINT",FACE,{"disambiguationData":[TD([[makeQuery(id+"F0.imprint","IMPRINT",EDGE,{"derivedFrom":sQuery(id+"F0.wireOp",EDGE,"E506")}),1.0]])]});
            var Q3;
            Q3=makeQuery(id+"F0.imprint","IMPRINT",FACE,{"disambiguationData":[TD([[makeQuery(id+"F0.imprint","IMPRINT",EDGE,{"derivedFrom":sQuery(id+"F0.wireOp",EDGE,"E28")}),1.0]])]});
            extrude(context, id + "F1", {"entities" : qUnion([Q0, Q1, Q2, Q3]), "depth" : 3 * mm, "offsetDistance" : 25 * mm});
        }
    });
